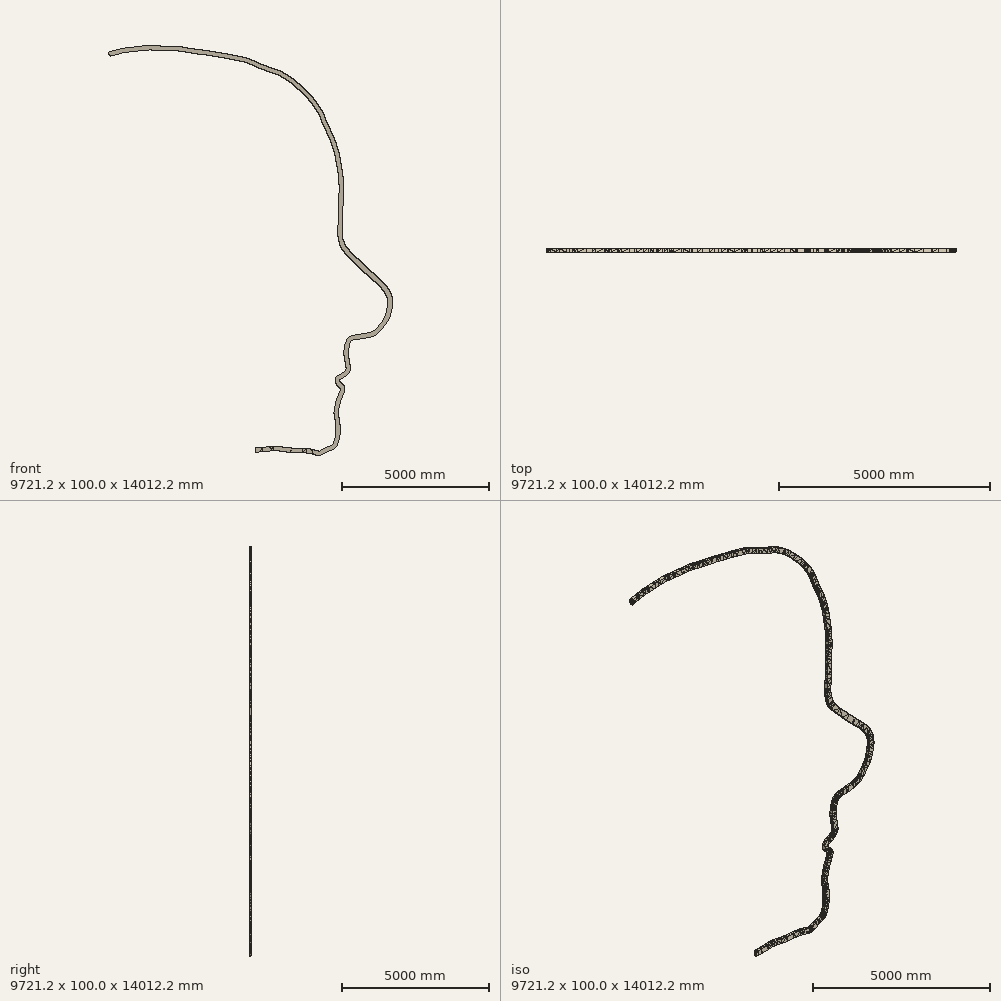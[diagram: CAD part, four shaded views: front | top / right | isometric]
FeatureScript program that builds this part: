
annotation { "Feature Type Name" : "Feature", "Feature Type Description" : "" }
export const myFeature = defineFeature(function(context is Context, id is Id, definition is map)
    precondition{}
    {
        {
            var Q0;
            Q0=qCreatedBy(makeId("Front.planeOp"),FACE);
            var sketch = newSketch(context, id + "F0", { "sketchPlane" : qUnion([Q0])});
            skLineSegment(sketch, "E0", {"start": v(3972.26, -824.32) * mm, "end": v(3779.27, -646.34) * mm});
            skLineSegment(sketch, "E1", {"start": v(3779.27, -646.34) * mm, "end": v(3769.31, -637.3) * mm});
            skLineSegment(sketch, "E2", {"start": v(3769.31, -637.3) * mm, "end": v(3603.88, -468.85) * mm});
            skLineSegment(sketch, "E3", {"start": v(3603.88, -468.85) * mm, "end": v(3566.98, -433.1) * mm});
            skLineSegment(sketch, "E4", {"start": v(3566.98, -433.1) * mm, "end": v(3382.58, -255.69) * mm});
            skLineSegment(sketch, "E5", {"start": v(3382.58, -255.69) * mm, "end": v(3380.14, -253.36) * mm});
            skLineSegment(sketch, "E6", {"start": v(3380.14, -253.36) * mm, "end": v(3227.02, -83.9) * mm});
            skLineSegment(sketch, "E7", {"start": v(3227.02, -83.9) * mm, "end": v(3181.68, -33.34) * mm});
            skLineSegment(sketch, "E8", {"start": v(3181.68, -33.34) * mm, "end": v(3138.16, 26.47) * mm});
            skLineSegment(sketch, "E9", {"start": v(3138.16, 26.47) * mm, "end": v(3127.38, 40.8) * mm});
            skLineSegment(sketch, "E10", {"start": v(3127.38, 40.8) * mm, "end": v(3121.17, 50.43) * mm});
            skLineSegment(sketch, "E11", {"start": v(3121.17, 50.43) * mm, "end": v(3079.1, 130.98) * mm});
            skLineSegment(sketch, "E12", {"start": v(3079.1, 130.98) * mm, "end": v(3056.52, 190.72) * mm});
            skLineSegment(sketch, "E13", {"start": v(3056.52, 190.72) * mm, "end": v(3014.85, 323.98) * mm});
            skLineSegment(sketch, "E14", {"start": v(3014.85, 323.98) * mm, "end": v(3003.42, 385.66) * mm});
            skLineSegment(sketch, "E15", {"start": v(3003.42, 385.66) * mm, "end": v(2997.38, 407.38) * mm});
            skLineSegment(sketch, "E16", {"start": v(2997.38, 407.38) * mm, "end": v(2980.84, 556.84) * mm});
            skLineSegment(sketch, "E17", {"start": v(2980.84, 556.84) * mm, "end": v(2980.65, 557.88) * mm});
            skLineSegment(sketch, "E18", {"start": v(2980.65, 557.88) * mm, "end": v(2980.53, 569.75) * mm});
            skLineSegment(sketch, "E19", {"start": v(2980.53, 569.75) * mm, "end": v(2979.3, 660.54) * mm});
            skLineSegment(sketch, "E20", {"start": v(2979.3, 660.54) * mm, "end": v(2980.22, 675.28) * mm});
            skLineSegment(sketch, "E21", {"start": v(2980.22, 675.28) * mm, "end": v(2979, 704.08) * mm});
            skLineSegment(sketch, "E22", {"start": v(2979, 704.08) * mm, "end": v(2991.56, 866.17) * mm});
            skLineSegment(sketch, "E23", {"start": v(2991.56, 866.17) * mm, "end": v(3001.68, 1021.18) * mm});
            skLineSegment(sketch, "E24", {"start": v(3001.68, 1021.18) * mm, "end": v(3005.61, 1150.84) * mm});
            skLineSegment(sketch, "E25", {"start": v(3005.61, 1150.84) * mm, "end": v(3008, 1205.13) * mm});
            skLineSegment(sketch, "E26", {"start": v(3008, 1205.13) * mm, "end": v(3007.86, 1232.13) * mm});
            skLineSegment(sketch, "E27", {"start": v(3007.86, 1232.13) * mm, "end": v(3008.6, 1500.34) * mm});
            skLineSegment(sketch, "E28", {"start": v(3008.6, 1500.34) * mm, "end": v(3010.72, 1635.8) * mm});
            skLineSegment(sketch, "E29", {"start": v(3010.72, 1635.8) * mm, "end": v(3011.72, 1678.4) * mm});
            skLineSegment(sketch, "E30", {"start": v(3011.72, 1678.4) * mm, "end": v(3016.1, 1776.05) * mm});
            skLineSegment(sketch, "E31", {"start": v(3016.1, 1776.05) * mm, "end": v(3023.13, 1920.29) * mm});
            skLineSegment(sketch, "E32", {"start": v(3023.13, 1920.29) * mm, "end": v(3028.4, 2010.83) * mm});
            skLineSegment(sketch, "E33", {"start": v(3028.4, 2010.83) * mm, "end": v(3029.3, 2054.07) * mm});
            skLineSegment(sketch, "E34", {"start": v(3029.3, 2054.07) * mm, "end": v(3028.87, 2105.86) * mm});
            skLineSegment(sketch, "E35", {"start": v(3028.87, 2105.86) * mm, "end": v(3028.95, 2113.76) * mm});
            skLineSegment(sketch, "E36", {"start": v(3028.95, 2113.76) * mm, "end": v(3028.93, 2114.83) * mm});
            skLineSegment(sketch, "E37", {"start": v(3028.93, 2114.83) * mm, "end": v(3028.85, 2117.34) * mm});
            skLineSegment(sketch, "E38", {"start": v(3028.85, 2117.34) * mm, "end": v(3028.63, 2122.4) * mm});
            skLineSegment(sketch, "E39", {"start": v(3028.63, 2122.4) * mm, "end": v(3025.85, 2236.85) * mm});
            skLineSegment(sketch, "E40", {"start": v(3025.85, 2236.85) * mm, "end": v(3019.27, 2333.14) * mm});
            skLineSegment(sketch, "E41", {"start": v(3019.27, 2333.14) * mm, "end": v(3014.35, 2454.84) * mm});
            skLineSegment(sketch, "E42", {"start": v(3014.35, 2454.84) * mm, "end": v(3009.17, 2525.23) * mm});
            skLineSegment(sketch, "E43", {"start": v(3009.17, 2525.23) * mm, "end": v(2999.77, 2601.55) * mm});
            skLineSegment(sketch, "E44", {"start": v(2999.77, 2601.55) * mm, "end": v(2999.15, 2606.38) * mm});
            skLineSegment(sketch, "E45", {"start": v(2999.15, 2606.38) * mm, "end": v(2996.37, 2623.67) * mm});
            skLineSegment(sketch, "E46", {"start": v(2996.37, 2623.67) * mm, "end": v(2939.92, 2948.67) * mm});
            skLineSegment(sketch, "E47", {"start": v(2939.92, 2948.67) * mm, "end": v(2924.68, 3037.87) * mm});
            skLineSegment(sketch, "E48", {"start": v(2924.68, 3037.87) * mm, "end": v(2915.3, 3107.38) * mm});
            skLineSegment(sketch, "E49", {"start": v(2915.3, 3107.38) * mm, "end": v(2889.1, 3252.45) * mm});
            skLineSegment(sketch, "E50", {"start": v(2889.1, 3252.45) * mm, "end": v(2884.6, 3279.42) * mm});
            skLineSegment(sketch, "E51", {"start": v(2884.6, 3279.42) * mm, "end": v(2875.96, 3316.34) * mm});
            skLineSegment(sketch, "E52", {"start": v(2875.96, 3316.34) * mm, "end": v(2876.2, 3313.02) * mm});
            skLineSegment(sketch, "E53", {"start": v(2876.2, 3313.02) * mm, "end": v(2867.58, 3345.82) * mm});
            skLineSegment(sketch, "E54", {"start": v(2867.58, 3345.82) * mm, "end": v(2844.67, 3415.38) * mm});
            skLineSegment(sketch, "E55", {"start": v(2844.67, 3415.38) * mm, "end": v(2827.61, 3467.45) * mm});
            skLineSegment(sketch, "E56", {"start": v(2827.61, 3467.45) * mm, "end": v(2812.09, 3521.46) * mm});
            skLineSegment(sketch, "E57", {"start": v(2812.09, 3521.46) * mm, "end": v(2797.48, 3569.06) * mm});
            skLineSegment(sketch, "E58", {"start": v(2797.48, 3569.06) * mm, "end": v(2765.14, 3666.56) * mm});
            skLineSegment(sketch, "E59", {"start": v(2765.14, 3666.56) * mm, "end": v(2742.38, 3726.82) * mm});
            skLineSegment(sketch, "E60", {"start": v(2742.38, 3726.82) * mm, "end": v(2725.35, 3770.91) * mm});
            skLineSegment(sketch, "E61", {"start": v(2725.35, 3770.91) * mm, "end": v(2656.42, 3924.3) * mm});
            skLineSegment(sketch, "E62", {"start": v(2656.42, 3924.3) * mm, "end": v(2639.9, 3958.92) * mm});
            skLineSegment(sketch, "E63", {"start": v(2639.9, 3958.92) * mm, "end": v(2633.1, 3973.99) * mm});
            skLineSegment(sketch, "E64", {"start": v(2633.1, 3973.99) * mm, "end": v(2613.84, 4015.32) * mm});
            skLineSegment(sketch, "E65", {"start": v(2613.84, 4015.32) * mm, "end": v(2589.35, 4066.77) * mm});
            skLineSegment(sketch, "E66", {"start": v(2589.35, 4066.77) * mm, "end": v(2556.64, 4136.94) * mm});
            skLineSegment(sketch, "E67", {"start": v(2556.64, 4136.94) * mm, "end": v(2547.28, 4156.79) * mm});
            skLineSegment(sketch, "E68", {"start": v(2547.28, 4156.79) * mm, "end": v(2545.41, 4160.18) * mm});
            skLineSegment(sketch, "E69", {"start": v(2545.41, 4160.18) * mm, "end": v(2530.68, 4192.32) * mm});
            skLineSegment(sketch, "E70", {"start": v(2530.68, 4192.32) * mm, "end": v(2526.52, 4196.93) * mm});
            skLineSegment(sketch, "E71", {"start": v(2526.52, 4196.93) * mm, "end": v(2511.45, 4227.76) * mm});
            skLineSegment(sketch, "E72", {"start": v(2511.45, 4227.76) * mm, "end": v(2492.95, 4272.02) * mm});
            skLineSegment(sketch, "E73", {"start": v(2492.95, 4272.02) * mm, "end": v(2457.92, 4357.18) * mm});
            skLineSegment(sketch, "E74", {"start": v(2457.92, 4357.18) * mm, "end": v(2429.87, 4423.94) * mm});
            skLineSegment(sketch, "E75", {"start": v(2429.87, 4423.94) * mm, "end": v(2428.51, 4428.26) * mm});
            skLineSegment(sketch, "E76", {"start": v(2428.51, 4428.26) * mm, "end": v(2407.27, 4484.6) * mm});
            skLineSegment(sketch, "E77", {"start": v(2407.27, 4484.6) * mm, "end": v(2367.75, 4583.7) * mm});
            skLineSegment(sketch, "E78", {"start": v(2367.75, 4583.7) * mm, "end": v(2350.04, 4623.65) * mm});
            skLineSegment(sketch, "E79", {"start": v(2350.04, 4623.65) * mm, "end": v(2340.66, 4642.93) * mm});
            skLineSegment(sketch, "E80", {"start": v(2340.66, 4642.93) * mm, "end": v(2310.55, 4699.05) * mm});
            skLineSegment(sketch, "E81", {"start": v(2310.55, 4699.05) * mm, "end": v(2289.12, 4737.81) * mm});
            skLineSegment(sketch, "E82", {"start": v(2289.12, 4737.81) * mm, "end": v(2281.78, 4750.14) * mm});
            skLineSegment(sketch, "E83", {"start": v(2281.78, 4750.14) * mm, "end": v(2253.96, 4793.21) * mm});
            skLineSegment(sketch, "E84", {"start": v(2253.96, 4793.21) * mm, "end": v(2166.56, 4923.2) * mm});
            skLineSegment(sketch, "E85", {"start": v(2166.56, 4923.2) * mm, "end": v(2158.06, 4935.64) * mm});
            skLineSegment(sketch, "E86", {"start": v(2158.06, 4935.64) * mm, "end": v(2083.12, 5033.59) * mm});
            skLineSegment(sketch, "E87", {"start": v(2083.12, 5033.59) * mm, "end": v(2056.5, 5068.4) * mm});
            skLineSegment(sketch, "E88", {"start": v(2056.5, 5068.4) * mm, "end": v(2022.08, 5111.38) * mm});
            skLineSegment(sketch, "E89", {"start": v(2022.08, 5111.38) * mm, "end": v(2006.56, 5130.31) * mm});
            skLineSegment(sketch, "E90", {"start": v(2006.56, 5130.31) * mm, "end": v(1938.82, 5208.36) * mm});
            skLineSegment(sketch, "E91", {"start": v(1938.82, 5208.36) * mm, "end": v(1900.64, 5249.8) * mm});
            skLineSegment(sketch, "E92", {"start": v(1900.64, 5249.8) * mm, "end": v(1723.26, 5424.37) * mm});
            skLineSegment(sketch, "E93", {"start": v(1723.26, 5424.37) * mm, "end": v(1663.3, 5482.42) * mm});
            skLineSegment(sketch, "E94", {"start": v(1663.3, 5482.42) * mm, "end": v(1639.5, 5504.81) * mm});
            skLineSegment(sketch, "E95", {"start": v(1639.5, 5504.81) * mm, "end": v(1621.41, 5520.52) * mm});
            skLineSegment(sketch, "E96", {"start": v(1621.41, 5520.52) * mm, "end": v(1477.89, 5651.1) * mm});
            skLineSegment(sketch, "E97", {"start": v(1477.89, 5651.1) * mm, "end": v(1449.95, 5675.24) * mm});
            skLineSegment(sketch, "E98", {"start": v(1449.95, 5675.24) * mm, "end": v(1383.35, 5730.76) * mm});
            skLineSegment(sketch, "E99", {"start": v(1383.35, 5730.76) * mm, "end": v(1311.46, 5784.69) * mm});
            skLineSegment(sketch, "E100", {"start": v(1311.46, 5784.69) * mm, "end": v(1296.05, 5795.72) * mm});
            skLineSegment(sketch, "E101", {"start": v(1296.05, 5795.72) * mm, "end": v(1258.83, 5818.84) * mm});
            skLineSegment(sketch, "E102", {"start": v(1258.83, 5818.84) * mm, "end": v(1223.82, 5839.55) * mm});
            skLineSegment(sketch, "E103", {"start": v(1223.82, 5839.55) * mm, "end": v(1193.56, 5858.43) * mm});
            skLineSegment(sketch, "E104", {"start": v(1193.56, 5858.43) * mm, "end": v(1062.64, 5937.28) * mm});
            skLineSegment(sketch, "E105", {"start": v(1062.64, 5937.28) * mm, "end": v(1018.58, 5963.58) * mm});
            skLineSegment(sketch, "E106", {"start": v(1018.58, 5963.58) * mm, "end": v(1007.24, 5969.89) * mm});
            skLineSegment(sketch, "E107", {"start": v(1007.24, 5969.89) * mm, "end": v(996.45, 5974.63) * mm});
            skLineSegment(sketch, "E108", {"start": v(996.45, 5974.63) * mm, "end": v(874.2, 6030.9) * mm});
            skLineSegment(sketch, "E109", {"start": v(874.2, 6030.9) * mm, "end": v(843.64, 6040.76) * mm});
            skLineSegment(sketch, "E110", {"start": v(843.64, 6040.76) * mm, "end": v(728.63, 6077.02) * mm});
            skLineSegment(sketch, "E111", {"start": v(728.63, 6077.02) * mm, "end": v(570.8, 6127.67) * mm});
            skLineSegment(sketch, "E112", {"start": v(570.8, 6127.67) * mm, "end": v(379.46, 6200) * mm});
            skLineSegment(sketch, "E113", {"start": v(379.46, 6200) * mm, "end": v(247.8, 6252.71) * mm});
            skLineSegment(sketch, "E114", {"start": v(247.8, 6252.71) * mm, "end": v(137.82, 6303.48) * mm});
            skLineSegment(sketch, "E115", {"start": v(137.82, 6303.48) * mm, "end": v(78.3, 6329.5) * mm});
            skLineSegment(sketch, "E116", {"start": v(78.3, 6329.5) * mm, "end": v(-31.33, 6375.46) * mm});
            skLineSegment(sketch, "E117", {"start": v(-31.33, 6375.46) * mm, "end": v(-46.3, 6381) * mm});
            skLineSegment(sketch, "E118", {"start": v(-46.3, 6381) * mm, "end": v(-181.75, 6432.14) * mm});
            skLineSegment(sketch, "E119", {"start": v(-181.75, 6432.14) * mm, "end": v(-182.38, 6432.34) * mm});
            skLineSegment(sketch, "E120", {"start": v(-182.38, 6432.34) * mm, "end": v(-259.74, 6454.73) * mm});
            skLineSegment(sketch, "E121", {"start": v(-259.74, 6454.73) * mm, "end": v(-363.85, 6475.57) * mm});
            skLineSegment(sketch, "E122", {"start": v(-363.85, 6475.57) * mm, "end": v(-548.48, 6513.3) * mm});
            skLineSegment(sketch, "E123", {"start": v(-548.48, 6513.3) * mm, "end": v(-606.65, 6527.06) * mm});
            skLineSegment(sketch, "E124", {"start": v(-606.65, 6527.06) * mm, "end": v(-794.8, 6560.9) * mm});
            skLineSegment(sketch, "E125", {"start": v(-794.8, 6560.9) * mm, "end": v(-826.95, 6566.3) * mm});
            skLineSegment(sketch, "E126", {"start": v(-826.95, 6566.3) * mm, "end": v(-882.75, 6576.29) * mm});
            skLineSegment(sketch, "E127", {"start": v(-882.75, 6576.29) * mm, "end": v(-1022.5, 6599.81) * mm});
            skLineSegment(sketch, "E128", {"start": v(-1022.5, 6599.81) * mm, "end": v(-1186.23, 6625.25) * mm});
            skLineSegment(sketch, "E129", {"start": v(-1186.23, 6625.25) * mm, "end": v(-1287.67, 6645.16) * mm});
            skLineSegment(sketch, "E130", {"start": v(-1287.67, 6645.16) * mm, "end": v(-1406.15, 6666.84) * mm});
            skLineSegment(sketch, "E131", {"start": v(-1406.15, 6666.84) * mm, "end": v(-1440.55, 6673.23) * mm});
            skLineSegment(sketch, "E132", {"start": v(-1440.55, 6673.23) * mm, "end": v(-1473.24, 6678.58) * mm});
            skLineSegment(sketch, "E133", {"start": v(-1473.24, 6678.58) * mm, "end": v(-1642.12, 6697.16) * mm});
            skLineSegment(sketch, "E134", {"start": v(-1642.12, 6697.16) * mm, "end": v(-1707, 6703.47) * mm});
            skLineSegment(sketch, "E135", {"start": v(-1707, 6703.47) * mm, "end": v(-1808.08, 6717.41) * mm});
            skLineSegment(sketch, "E136", {"start": v(-1808.08, 6717.41) * mm, "end": v(-1881.54, 6729.07) * mm});
            skLineSegment(sketch, "E137", {"start": v(-1881.54, 6729.07) * mm, "end": v(-1961.81, 6741.61) * mm});
            skLineSegment(sketch, "E138", {"start": v(-1961.81, 6741.61) * mm, "end": v(-2040.41, 6753.86) * mm});
            skLineSegment(sketch, "E139", {"start": v(-2040.41, 6753.86) * mm, "end": v(-2094.47, 6762.39) * mm});
            skLineSegment(sketch, "E140", {"start": v(-2094.47, 6762.39) * mm, "end": v(-2141.2, 6766.92) * mm});
            skLineSegment(sketch, "E141", {"start": v(-2141.2, 6766.92) * mm, "end": v(-2227, 6781.64) * mm});
            skLineSegment(sketch, "E142", {"start": v(-2227, 6781.64) * mm, "end": v(-2287.4, 6794.93) * mm});
            skLineSegment(sketch, "E143", {"start": v(-2287.4, 6794.93) * mm, "end": v(-2337.03, 6805.41) * mm});
            skLineSegment(sketch, "E144", {"start": v(-2337.03, 6805.41) * mm, "end": v(-2351.85, 6807.81) * mm});
            skLineSegment(sketch, "E145", {"start": v(-2351.85, 6807.81) * mm, "end": v(-2404.98, 6813.57) * mm});
            skLineSegment(sketch, "E146", {"start": v(-2404.98, 6813.57) * mm, "end": v(-2463.72, 6818.16) * mm});
            skLineSegment(sketch, "E147", {"start": v(-2463.72, 6818.16) * mm, "end": v(-2571.94, 6818.85) * mm});
            skLineSegment(sketch, "E148", {"start": v(-2571.94, 6818.85) * mm, "end": v(-2731.8, 6826.28) * mm});
            skLineSegment(sketch, "E149", {"start": v(-2731.8, 6826.28) * mm, "end": v(-2785.54, 6829.65) * mm});
            skLineSegment(sketch, "E150", {"start": v(-2785.54, 6829.65) * mm, "end": v(-2889.66, 6832.45) * mm});
            skLineSegment(sketch, "E151", {"start": v(-2889.66, 6832.45) * mm, "end": v(-2892.43, 6832.55) * mm});
            skLineSegment(sketch, "E152", {"start": v(-2892.43, 6832.55) * mm, "end": v(-2894.79, 6832.54) * mm});
            skLineSegment(sketch, "E153", {"start": v(-2894.79, 6832.54) * mm, "end": v(-2895.37, 6832.5) * mm});
            skLineSegment(sketch, "E154", {"start": v(-2895.37, 6832.5) * mm, "end": v(-2911.65, 6832.88) * mm});
            skLineSegment(sketch, "E155", {"start": v(-2911.65, 6832.88) * mm, "end": v(-3119.59, 6837.72) * mm});
            skLineSegment(sketch, "E156", {"start": v(-3119.59, 6837.72) * mm, "end": v(-3152.58, 6839.85) * mm});
            skLineSegment(sketch, "E157", {"start": v(-3152.58, 6839.85) * mm, "end": v(-3163.88, 6839.74) * mm});
            skLineSegment(sketch, "E158", {"start": v(-3163.88, 6839.74) * mm, "end": v(-3340.1, 6850.89) * mm});
            skLineSegment(sketch, "E159", {"start": v(-3340.1, 6850.89) * mm, "end": v(-3388.5, 6852.77) * mm});
            skLineSegment(sketch, "E160", {"start": v(-3388.5, 6852.77) * mm, "end": v(-3406.3, 6853.9) * mm});
            skLineSegment(sketch, "E161", {"start": v(-3406.3, 6853.9) * mm, "end": v(-3458.98, 6852.25) * mm});
            skLineSegment(sketch, "E162", {"start": v(-3458.98, 6852.25) * mm, "end": v(-3470.61, 6851.67) * mm});
            skLineSegment(sketch, "E163", {"start": v(-3470.61, 6851.67) * mm, "end": v(-3673.53, 6836.83) * mm});
            skLineSegment(sketch, "E164", {"start": v(-3673.53, 6836.83) * mm, "end": v(-3756.56, 6824.4) * mm});
            skLineSegment(sketch, "E165", {"start": v(-3756.56, 6824.4) * mm, "end": v(-3899, 6810.6) * mm});
            skLineSegment(sketch, "E166", {"start": v(-3899, 6810.6) * mm, "end": v(-4117.06, 6784.5) * mm});
            skLineSegment(sketch, "E167", {"start": v(-4117.06, 6784.5) * mm, "end": v(-4167.83, 6781.03) * mm});
            skLineSegment(sketch, "E168", {"start": v(-4167.83, 6781.03) * mm, "end": v(-4209.42, 6776.17) * mm});
            skLineSegment(sketch, "E169", {"start": v(-4209.42, 6776.17) * mm, "end": v(-4281.01, 6766.82) * mm});
            skLineSegment(sketch, "E170", {"start": v(-4281.01, 6766.82) * mm, "end": v(-4355.94, 6750.4) * mm});
            skLineSegment(sketch, "E171", {"start": v(-4355.94, 6750.4) * mm, "end": v(-4520.42, 6707.77) * mm});
            skLineSegment(sketch, "E172", {"start": v(-4520.42, 6707.77) * mm, "end": v(-4577.1, 6695.55) * mm});
            skLineSegment(sketch, "E173", {"start": v(-4577.1, 6695.55) * mm, "end": v(-4716.45, 6658.86) * mm});
            skLineSegment(sketch, "E174", {"start": v(-4716.45, 6658.86) * mm, "end": v(-4753.97, 6640.97) * mm});
            skLineSegment(sketch, "E175", {"start": v(-4753.97, 6640.97) * mm, "end": v(-4781.21, 6630.5) * mm});
            skLineSegment(sketch, "E176", {"start": v(-4781.21, 6630.5) * mm, "end": v(-4785.2, 6624.34) * mm});
            skLineSegment(sketch, "E177", {"start": v(-4785.2, 6624.34) * mm, "end": v(-4836.21, 6708.52) * mm});
            skLineSegment(sketch, "E178", {"start": v(-4836.21, 6708.52) * mm, "end": v(-4860.6, 6756.23) * mm});
            skLineSegment(sketch, "E179", {"start": v(-4860.6, 6756.23) * mm, "end": v(-4838, 6770.7) * mm});
            skLineSegment(sketch, "E180", {"start": v(-4838, 6770.7) * mm, "end": v(-4808.5, 6782.56) * mm});
            skLineSegment(sketch, "E181", {"start": v(-4808.5, 6782.56) * mm, "end": v(-4766.09, 6802.5) * mm});
            skLineSegment(sketch, "E182", {"start": v(-4766.09, 6802.5) * mm, "end": v(-4624.14, 6840.4) * mm});
            skLineSegment(sketch, "E183", {"start": v(-4624.14, 6840.4) * mm, "end": v(-4559.22, 6854.74) * mm});
            skLineSegment(sketch, "E184", {"start": v(-4559.22, 6854.74) * mm, "end": v(-4385.23, 6899.7) * mm});
            skLineSegment(sketch, "E185", {"start": v(-4385.23, 6899.7) * mm, "end": v(-4308.9, 6916.34) * mm});
            skLineSegment(sketch, "E186", {"start": v(-4308.9, 6916.34) * mm, "end": v(-4235.61, 6926.03) * mm});
            skLineSegment(sketch, "E187", {"start": v(-4235.61, 6926.03) * mm, "end": v(-4185.73, 6932.05) * mm});
            skLineSegment(sketch, "E188", {"start": v(-4185.73, 6932.05) * mm, "end": v(-4130.51, 6935.84) * mm});
            skLineSegment(sketch, "E189", {"start": v(-4130.51, 6935.84) * mm, "end": v(-3917.79, 6961.37) * mm});
            skLineSegment(sketch, "E190", {"start": v(-3917.79, 6961.37) * mm, "end": v(-3774.75, 6975.23) * mm});
            skLineSegment(sketch, "E191", {"start": v(-3774.75, 6975.23) * mm, "end": v(-3687.56, 6988.27) * mm});
            skLineSegment(sketch, "E192", {"start": v(-3687.56, 6988.27) * mm, "end": v(-3481.47, 7003.25) * mm});
            skLineSegment(sketch, "E193", {"start": v(-3481.47, 7003.25) * mm, "end": v(-3465.48, 7004.02) * mm});
            skLineSegment(sketch, "E194", {"start": v(-3465.48, 7004.02) * mm, "end": v(-3400.75, 7006.12) * mm});
            skLineSegment(sketch, "E195", {"start": v(-3400.75, 7006.12) * mm, "end": v(-3376.14, 7004.65) * mm});
            skLineSegment(sketch, "E196", {"start": v(-3376.14, 7004.65) * mm, "end": v(-3321.2, 7002.45) * mm});
            skLineSegment(sketch, "E197", {"start": v(-3321.2, 7002.45) * mm, "end": v(-3165.98, 6992.82) * mm});
            skLineSegment(sketch, "E198", {"start": v(-3165.98, 6992.82) * mm, "end": v(-3147.76, 6992.87) * mm});
            skLineSegment(sketch, "E199", {"start": v(-3147.76, 6992.87) * mm, "end": v(-3093.06, 6989.5) * mm});
            skLineSegment(sketch, "E200", {"start": v(-3093.06, 6989.5) * mm, "end": v(-2890.67, 6984.7) * mm});
            skLineSegment(sketch, "E201", {"start": v(-2890.67, 6984.7) * mm, "end": v(-2886.25, 6984.41) * mm});
            skLineSegment(sketch, "E202", {"start": v(-2886.25, 6984.41) * mm, "end": v(-2778.13, 6981.43) * mm});
            skLineSegment(sketch, "E203", {"start": v(-2778.13, 6981.43) * mm, "end": v(-2724.61, 6978.09) * mm});
            skLineSegment(sketch, "E204", {"start": v(-2724.61, 6978.09) * mm, "end": v(-2563.57, 6970.6) * mm});
            skLineSegment(sketch, "E205", {"start": v(-2563.57, 6970.6) * mm, "end": v(-2453.66, 6969.8) * mm});
            skLineSegment(sketch, "E206", {"start": v(-2453.66, 6969.8) * mm, "end": v(-2391.62, 6965.07) * mm});
            skLineSegment(sketch, "E207", {"start": v(-2391.62, 6965.07) * mm, "end": v(-2333.64, 6958.7) * mm});
            skLineSegment(sketch, "E208", {"start": v(-2333.64, 6958.7) * mm, "end": v(-2314.67, 6955.77) * mm});
            skLineSegment(sketch, "E209", {"start": v(-2314.67, 6955.77) * mm, "end": v(-2252.48, 6942.95) * mm});
            skLineSegment(sketch, "E210", {"start": v(-2252.48, 6942.95) * mm, "end": v(-2243.27, 6940.75) * mm});
            skLineSegment(sketch, "E211", {"start": v(-2243.27, 6940.75) * mm, "end": v(-2235.14, 6939.12) * mm});
            skLineSegment(sketch, "E212", {"start": v(-2235.14, 6939.12) * mm, "end": v(-2209.97, 6932.95) * mm});
            skLineSegment(sketch, "E213", {"start": v(-2209.97, 6932.95) * mm, "end": v(-2120.78, 6917.8) * mm});
            skLineSegment(sketch, "E214", {"start": v(-2120.78, 6917.8) * mm, "end": v(-2067.48, 6912.55) * mm});
            skLineSegment(sketch, "E215", {"start": v(-2067.48, 6912.55) * mm, "end": v(-1994.56, 6901.4) * mm});
            skLineSegment(sketch, "E216", {"start": v(-1994.56, 6901.4) * mm, "end": v(-1937.85, 6892.66) * mm});
            skLineSegment(sketch, "E217", {"start": v(-1937.85, 6892.66) * mm, "end": v(-1887.07, 6884.72) * mm});
            skLineSegment(sketch, "E218", {"start": v(-1887.07, 6884.72) * mm, "end": v(-1843.44, 6877.78) * mm});
            skLineSegment(sketch, "E219", {"start": v(-1843.44, 6877.78) * mm, "end": v(-1666.55, 6853.38) * mm});
            skLineSegment(sketch, "E220", {"start": v(-1666.55, 6853.38) * mm, "end": v(-1612.62, 6848.12) * mm});
            skLineSegment(sketch, "E221", {"start": v(-1612.62, 6848.12) * mm, "end": v(-1462.66, 6831.54) * mm});
            skLineSegment(sketch, "E222", {"start": v(-1462.66, 6831.54) * mm, "end": v(-1420.8, 6824.61) * mm});
            skLineSegment(sketch, "E223", {"start": v(-1420.8, 6824.61) * mm, "end": v(-1387.14, 6818.34) * mm});
            skLineSegment(sketch, "E224", {"start": v(-1387.14, 6818.34) * mm, "end": v(-1276.88, 6798.22) * mm});
            skLineSegment(sketch, "E225", {"start": v(-1276.88, 6798.22) * mm, "end": v(-1165.94, 6776.41) * mm});
            skLineSegment(sketch, "E226", {"start": v(-1165.94, 6776.41) * mm, "end": v(-994.2, 6749.77) * mm});
            skLineSegment(sketch, "E227", {"start": v(-994.2, 6749.77) * mm, "end": v(-873.37, 6729.55) * mm});
            skLineSegment(sketch, "E228", {"start": v(-873.37, 6729.55) * mm, "end": v(-779.05, 6712.59) * mm});
            skLineSegment(sketch, "E229", {"start": v(-779.05, 6712.59) * mm, "end": v(-715.43, 6701.98) * mm});
            skLineSegment(sketch, "E230", {"start": v(-715.43, 6701.98) * mm, "end": v(-578.02, 6677.21) * mm});
            skLineSegment(sketch, "E231", {"start": v(-578.02, 6677.21) * mm, "end": v(-535.65, 6667.2) * mm});
            skLineSegment(sketch, "E232", {"start": v(-535.65, 6667.2) * mm, "end": v(-414.65, 6642.48) * mm});
            skLineSegment(sketch, "E233", {"start": v(-414.65, 6642.48) * mm, "end": v(-235.25, 6606.4) * mm});
            skLineSegment(sketch, "E234", {"start": v(-235.25, 6606.4) * mm, "end": v(-163.46, 6585.66) * mm});
            skLineSegment(sketch, "E235", {"start": v(-163.46, 6585.66) * mm, "end": v(-130.47, 6574.9) * mm});
            skLineSegment(sketch, "E236", {"start": v(-130.47, 6574.9) * mm, "end": v(-85.68, 6558.84) * mm});
            skLineSegment(sketch, "E237", {"start": v(-85.68, 6558.84) * mm, "end": v(6.54, 6524.01) * mm});
            skLineSegment(sketch, "E238", {"start": v(6.54, 6524.01) * mm, "end": v(17.88, 6519.82) * mm});
            skLineSegment(sketch, "E239", {"start": v(17.88, 6519.82) * mm, "end": v(143.06, 6467.33) * mm});
            skLineSegment(sketch, "E240", {"start": v(143.06, 6467.33) * mm, "end": v(214.58, 6436.17) * mm});
            skLineSegment(sketch, "E241", {"start": v(214.58, 6436.17) * mm, "end": v(307.4, 6393.35) * mm});
            skLineSegment(sketch, "E242", {"start": v(307.4, 6393.35) * mm, "end": v(455.51, 6333.96) * mm});
            skLineSegment(sketch, "E243", {"start": v(455.51, 6333.96) * mm, "end": v(626.5, 6269.4) * mm});
            skLineSegment(sketch, "E244", {"start": v(626.5, 6269.4) * mm, "end": v(771.62, 6222.91) * mm});
            skLineSegment(sketch, "E245", {"start": v(771.62, 6222.91) * mm, "end": v(913.5, 6177.84) * mm});
            skLineSegment(sketch, "E246", {"start": v(913.5, 6177.84) * mm, "end": v(935.4, 6170.64) * mm});
            skLineSegment(sketch, "E247", {"start": v(935.4, 6170.64) * mm, "end": v(1036.9, 6123.97) * mm});
            skLineSegment(sketch, "E248", {"start": v(1036.9, 6123.97) * mm, "end": v(1077.9, 6104.5) * mm});
            skLineSegment(sketch, "E249", {"start": v(1077.9, 6104.5) * mm, "end": v(1084.59, 6101.03) * mm});
            skLineSegment(sketch, "E250", {"start": v(1084.59, 6101.03) * mm, "end": v(1268.15, 5990.84) * mm});
            skLineSegment(sketch, "E251", {"start": v(1268.15, 5990.84) * mm, "end": v(1303.74, 5968.64) * mm});
            skLineSegment(sketch, "E252", {"start": v(1303.74, 5968.64) * mm, "end": v(1343.26, 5945.28) * mm});
            skLineSegment(sketch, "E253", {"start": v(1343.26, 5945.28) * mm, "end": v(1379.97, 5922.38) * mm});
            skLineSegment(sketch, "E254", {"start": v(1379.97, 5922.38) * mm, "end": v(1398.78, 5908.94) * mm});
            skLineSegment(sketch, "E255", {"start": v(1398.78, 5908.94) * mm, "end": v(1476.7, 5850.65) * mm});
            skLineSegment(sketch, "E256", {"start": v(1476.7, 5850.65) * mm, "end": v(1546.2, 5792.8) * mm});
            skLineSegment(sketch, "E257", {"start": v(1546.2, 5792.8) * mm, "end": v(1577.24, 5766.04) * mm});
            skLineSegment(sketch, "E258", {"start": v(1577.24, 5766.04) * mm, "end": v(1726.03, 5630.73) * mm});
            skLineSegment(sketch, "E259", {"start": v(1726.03, 5630.73) * mm, "end": v(1744.2, 5614.98) * mm});
            skLineSegment(sketch, "E260", {"start": v(1744.2, 5614.98) * mm, "end": v(1768.06, 5592.53) * mm});
            skLineSegment(sketch, "E261", {"start": v(1768.06, 5592.53) * mm, "end": v(1826.25, 5536.15) * mm});
            skLineSegment(sketch, "E262", {"start": v(1826.25, 5536.15) * mm, "end": v(2010.72, 5354.47) * mm});
            skLineSegment(sketch, "E263", {"start": v(2010.72, 5354.47) * mm, "end": v(2051.65, 5310.03) * mm});
            skLineSegment(sketch, "E264", {"start": v(2051.65, 5310.03) * mm, "end": v(2123.02, 5227.87) * mm});
            skLineSegment(sketch, "E265", {"start": v(2123.02, 5227.87) * mm, "end": v(2140.47, 5206.58) * mm});
            skLineSegment(sketch, "E266", {"start": v(2140.47, 5206.58) * mm, "end": v(2180.37, 5156.73) * mm});
            skLineSegment(sketch, "E267", {"start": v(2180.37, 5156.73) * mm, "end": v(2211.35, 5116.18) * mm});
            skLineSegment(sketch, "E268", {"start": v(2211.35, 5116.18) * mm, "end": v(2283.16, 5022.36) * mm});
            skLineSegment(sketch, "E269", {"start": v(2283.16, 5022.36) * mm, "end": v(2297.27, 5001.74) * mm});
            skLineSegment(sketch, "E270", {"start": v(2297.27, 5001.74) * mm, "end": v(2381.67, 4876.15) * mm});
            skLineSegment(sketch, "E271", {"start": v(2381.67, 4876.15) * mm, "end": v(2412.92, 4827.8) * mm});
            skLineSegment(sketch, "E272", {"start": v(2412.92, 4827.8) * mm, "end": v(2419.29, 4817.07) * mm});
            skLineSegment(sketch, "E273", {"start": v(2419.29, 4817.07) * mm, "end": v(2444.6, 4771.25) * mm});
            skLineSegment(sketch, "E274", {"start": v(2444.6, 4771.25) * mm, "end": v(2473.9, 4716.62) * mm});
            skLineSegment(sketch, "E275", {"start": v(2473.9, 4716.62) * mm, "end": v(2486.81, 4690.02) * mm});
            skLineSegment(sketch, "E276", {"start": v(2486.81, 4690.02) * mm, "end": v(2505.99, 4646.98) * mm});
            skLineSegment(sketch, "E277", {"start": v(2505.99, 4646.98) * mm, "end": v(2546.64, 4545.33) * mm});
            skLineSegment(sketch, "E278", {"start": v(2546.64, 4545.33) * mm, "end": v(2568.9, 4486.45) * mm});
            skLineSegment(sketch, "E279", {"start": v(2568.9, 4486.45) * mm, "end": v(2570.77, 4480.84) * mm});
            skLineSegment(sketch, "E280", {"start": v(2570.77, 4480.84) * mm, "end": v(2598.22, 4415.59) * mm});
            skLineSegment(sketch, "E281", {"start": v(2598.22, 4415.59) * mm, "end": v(2636.96, 4319.55) * mm});
            skLineSegment(sketch, "E282", {"start": v(2636.96, 4319.55) * mm, "end": v(2646.58, 4296.3) * mm});
            skLineSegment(sketch, "E283", {"start": v(2646.58, 4296.3) * mm, "end": v(2655.98, 4277.27) * mm});
            skLineSegment(sketch, "E284", {"start": v(2655.98, 4277.27) * mm, "end": v(2668.1, 4257.22) * mm});
            skLineSegment(sketch, "E285", {"start": v(2668.1, 4257.22) * mm, "end": v(2682.16, 4226.51) * mm});
            skLineSegment(sketch, "E286", {"start": v(2682.16, 4226.51) * mm, "end": v(2684.11, 4222.93) * mm});
            skLineSegment(sketch, "E287", {"start": v(2684.11, 4222.93) * mm, "end": v(2693.83, 4202.35) * mm});
            skLineSegment(sketch, "E288", {"start": v(2693.83, 4202.35) * mm, "end": v(2727.43, 4130.28) * mm});
            skLineSegment(sketch, "E289", {"start": v(2727.43, 4130.28) * mm, "end": v(2752.37, 4077.86) * mm});
            skLineSegment(sketch, "E290", {"start": v(2752.37, 4077.86) * mm, "end": v(2771.29, 4037.28) * mm});
            skLineSegment(sketch, "E291", {"start": v(2771.29, 4037.28) * mm, "end": v(2778.06, 4022.24) * mm});
            skLineSegment(sketch, "E292", {"start": v(2778.06, 4022.24) * mm, "end": v(2794.6, 3987.5) * mm});
            skLineSegment(sketch, "E293", {"start": v(2794.6, 3987.5) * mm, "end": v(2865.8, 3828.97) * mm});
            skLineSegment(sketch, "E294", {"start": v(2865.8, 3828.97) * mm, "end": v(2884.55, 3780.4) * mm});
            skLineSegment(sketch, "E295", {"start": v(2884.55, 3780.4) * mm, "end": v(2908.67, 3716.52) * mm});
            skLineSegment(sketch, "E296", {"start": v(2908.67, 3716.52) * mm, "end": v(2942, 3616.03) * mm});
            skLineSegment(sketch, "E297", {"start": v(2942, 3616.03) * mm, "end": v(2957.05, 3567.11) * mm});
            skLineSegment(sketch, "E298", {"start": v(2957.05, 3567.11) * mm, "end": v(2972.44, 3513.62) * mm});
            skLineSegment(sketch, "E299", {"start": v(2972.44, 3513.62) * mm, "end": v(2990.34, 3458.78) * mm});
            skLineSegment(sketch, "E300", {"start": v(2990.34, 3458.78) * mm, "end": v(3010.94, 3395.47) * mm});
            skLineSegment(sketch, "E301", {"start": v(3010.94, 3395.47) * mm, "end": v(3021.35, 3356.3) * mm});
            skLineSegment(sketch, "E302", {"start": v(3021.35, 3356.3) * mm, "end": v(3023.68, 3351.77) * mm});
            skLineSegment(sketch, "E303", {"start": v(3023.68, 3351.77) * mm, "end": v(3033.15, 3311.43) * mm});
            skLineSegment(sketch, "E304", {"start": v(3033.15, 3311.43) * mm, "end": v(3038.1, 3281.95) * mm});
            skLineSegment(sketch, "E305", {"start": v(3038.1, 3281.95) * mm, "end": v(3065.23, 3132.22) * mm});
            skLineSegment(sketch, "E306", {"start": v(3065.23, 3132.22) * mm, "end": v(3074.16, 3066.12) * mm});
            skLineSegment(sketch, "E307", {"start": v(3074.16, 3066.12) * mm, "end": v(3089.7, 2975.26) * mm});
            skLineSegment(sketch, "E308", {"start": v(3089.7, 2975.26) * mm, "end": v(3144.9, 2657.36) * mm});
            skLineSegment(sketch, "E309", {"start": v(3144.9, 2657.36) * mm, "end": v(3149.57, 2628.3) * mm});
            skLineSegment(sketch, "E310", {"start": v(3149.57, 2628.3) * mm, "end": v(3150.69, 2619.46) * mm});
            skLineSegment(sketch, "E311", {"start": v(3150.69, 2619.46) * mm, "end": v(3160.52, 2539.5) * mm});
            skLineSegment(sketch, "E312", {"start": v(3160.52, 2539.5) * mm, "end": v(3165.82, 2467.58) * mm});
            skLineSegment(sketch, "E313", {"start": v(3165.82, 2467.58) * mm, "end": v(3170.96, 2342.22) * mm});
            skLineSegment(sketch, "E314", {"start": v(3170.96, 2342.22) * mm, "end": v(3177.75, 2242.37) * mm});
            skLineSegment(sketch, "E315", {"start": v(3177.75, 2242.37) * mm, "end": v(3180.5, 2130.7) * mm});
            skLineSegment(sketch, "E316", {"start": v(3180.5, 2130.7) * mm, "end": v(3180.9, 2121.35) * mm});
            skLineSegment(sketch, "E317", {"start": v(3180.9, 2121.35) * mm, "end": v(3181.04, 2116.82) * mm});
            skLineSegment(sketch, "E318", {"start": v(3181.04, 2116.82) * mm, "end": v(3181.09, 2114.85) * mm});
            skLineSegment(sketch, "E319", {"start": v(3181.09, 2114.85) * mm, "end": v(3180.93, 2099.43) * mm});
            skLineSegment(sketch, "E320", {"start": v(3180.93, 2099.43) * mm, "end": v(3181.27, 2047.07) * mm});
            skLineSegment(sketch, "E321", {"start": v(3181.27, 2047.07) * mm, "end": v(3180.47, 2007.94) * mm});
            skLineSegment(sketch, "E322", {"start": v(3180.47, 2007.94) * mm, "end": v(3175.78, 1927) * mm});
            skLineSegment(sketch, "E323", {"start": v(3175.78, 1927) * mm, "end": v(3170.05, 1809.32) * mm});
            skLineSegment(sketch, "E324", {"start": v(3170.05, 1809.32) * mm, "end": v(3164.32, 1681.54) * mm});
            skLineSegment(sketch, "E325", {"start": v(3164.32, 1681.54) * mm, "end": v(3162.98, 1624.55) * mm});
            skLineSegment(sketch, "E326", {"start": v(3162.98, 1624.55) * mm, "end": v(3161, 1496.73) * mm});
            skLineSegment(sketch, "E327", {"start": v(3161, 1496.73) * mm, "end": v(3160.29, 1238.83) * mm});
            skLineSegment(sketch, "E328", {"start": v(3160.29, 1238.83) * mm, "end": v(3160.49, 1201.04) * mm});
            skLineSegment(sketch, "E329", {"start": v(3160.49, 1201.04) * mm, "end": v(3157.13, 1125) * mm});
            skLineSegment(sketch, "E330", {"start": v(3157.13, 1125) * mm, "end": v(3153.66, 1011.3) * mm});
            skLineSegment(sketch, "E331", {"start": v(3153.66, 1011.3) * mm, "end": v(3142.8, 846.75) * mm});
            skLineSegment(sketch, "E332", {"start": v(3142.8, 846.75) * mm, "end": v(3130.83, 693.78) * mm});
            skLineSegment(sketch, "E333", {"start": v(3130.83, 693.78) * mm, "end": v(3132.47, 674.33) * mm});
            skLineSegment(sketch, "E334", {"start": v(3132.47, 674.33) * mm, "end": v(3132.06, 667.94) * mm});
            skLineSegment(sketch, "E335", {"start": v(3132.06, 667.94) * mm, "end": v(3132.56, 636.34) * mm});
            skLineSegment(sketch, "E336", {"start": v(3132.56, 636.34) * mm, "end": v(3133.12, 561.3) * mm});
            skLineSegment(sketch, "E337", {"start": v(3133.12, 561.3) * mm, "end": v(3134.44, 554.35) * mm});
            skLineSegment(sketch, "E338", {"start": v(3134.44, 554.35) * mm, "end": v(3146.22, 440.9) * mm});
            skLineSegment(sketch, "E339", {"start": v(3146.22, 440.9) * mm, "end": v(3167.3, 366.4) * mm});
            skLineSegment(sketch, "E340", {"start": v(3167.3, 366.4) * mm, "end": v(3169.02, 361.7) * mm});
            skLineSegment(sketch, "E341", {"start": v(3169.02, 361.7) * mm, "end": v(3220, 224.52) * mm});
            skLineSegment(sketch, "E342", {"start": v(3220, 224.52) * mm, "end": v(3234.98, 190.89) * mm});
            skLineSegment(sketch, "E343", {"start": v(3234.98, 190.89) * mm, "end": v(3296.43, 104.79) * mm});
            skLineSegment(sketch, "E344", {"start": v(3296.43, 104.79) * mm, "end": v(3309.3, 85.1) * mm});
            skLineSegment(sketch, "E345", {"start": v(3309.3, 85.1) * mm, "end": v(3311.9, 81.67) * mm});
            skLineSegment(sketch, "E346", {"start": v(3311.9, 81.67) * mm, "end": v(3323.17, 69.05) * mm});
            skLineSegment(sketch, "E347", {"start": v(3323.17, 69.05) * mm, "end": v(3514.53, -146.86) * mm});
            skLineSegment(sketch, "E348", {"start": v(3514.53, -146.86) * mm, "end": v(3686.62, -298.48) * mm});
            skLineSegment(sketch, "E349", {"start": v(3686.62, -298.48) * mm, "end": v(3720.82, -331.45) * mm});
            skLineSegment(sketch, "E350", {"start": v(3720.82, -331.45) * mm, "end": v(3862.91, -468.24) * mm});
            skLineSegment(sketch, "E351", {"start": v(3862.91, -468.24) * mm, "end": v(3863.64, -468.98) * mm});
            skLineSegment(sketch, "E352", {"start": v(3863.64, -468.98) * mm, "end": v(3864.95, -470.17) * mm});
            skLineSegment(sketch, "E353", {"start": v(3864.95, -470.17) * mm, "end": v(4083.56, -675.75) * mm});
            skLineSegment(sketch, "E354", {"start": v(4083.56, -675.75) * mm, "end": v(4274.28, -846.78) * mm});
            skLineSegment(sketch, "E355", {"start": v(4274.28, -846.78) * mm, "end": v(4274.88, -847.33) * mm});
            skLineSegment(sketch, "E356", {"start": v(4274.88, -847.33) * mm, "end": v(4275.2, -847.6) * mm});
            skLineSegment(sketch, "E357", {"start": v(4275.2, -847.6) * mm, "end": v(4275.41, -847.8) * mm});
            skLineSegment(sketch, "E358", {"start": v(4275.41, -847.8) * mm, "end": v(4280.47, -852.28) * mm});
            skLineSegment(sketch, "E359", {"start": v(4280.47, -852.28) * mm, "end": v(4439.84, -994.84) * mm});
            skLineSegment(sketch, "E360", {"start": v(4439.84, -994.84) * mm, "end": v(4617.47, -1183.49) * mm});
            skLineSegment(sketch, "E361", {"start": v(4617.47, -1183.49) * mm, "end": v(4627.35, -1193.8) * mm});
            skLineSegment(sketch, "E362", {"start": v(4627.35, -1193.8) * mm, "end": v(4633.53, -1200.5) * mm});
            skLineSegment(sketch, "E363", {"start": v(4633.53, -1200.5) * mm, "end": v(4696.22, -1285.61) * mm});
            skLineSegment(sketch, "E364", {"start": v(4696.22, -1285.61) * mm, "end": v(4720.3, -1320) * mm});
            skLineSegment(sketch, "E365", {"start": v(4720.3, -1320) * mm, "end": v(4733.12, -1341.1) * mm});
            skLineSegment(sketch, "E366", {"start": v(4733.12, -1341.1) * mm, "end": v(4793, -1457.4) * mm});
            skLineSegment(sketch, "E367", {"start": v(4793, -1457.4) * mm, "end": v(4797.06, -1467.24) * mm});
            skLineSegment(sketch, "E368", {"start": v(4797.06, -1467.24) * mm, "end": v(4829.48, -1560.55) * mm});
            skLineSegment(sketch, "E369", {"start": v(4829.48, -1560.55) * mm, "end": v(4841.35, -1601.8) * mm});
            skLineSegment(sketch, "E370", {"start": v(4841.35, -1601.8) * mm, "end": v(4850.91, -1650.2) * mm});
            skLineSegment(sketch, "E371", {"start": v(4850.91, -1650.2) * mm, "end": v(4859.5, -1698.95) * mm});
            skLineSegment(sketch, "E372", {"start": v(4859.5, -1698.95) * mm, "end": v(4859.2, -1708.22) * mm});
            skLineSegment(sketch, "E373", {"start": v(4859.2, -1708.22) * mm, "end": v(4860.06, -1789.7) * mm});
            skLineSegment(sketch, "E374", {"start": v(4860.06, -1789.7) * mm, "end": v(4860.6, -1853.57) * mm});
            skLineSegment(sketch, "E375", {"start": v(4860.6, -1853.57) * mm, "end": v(4859.43, -1875.64) * mm});
            skLineSegment(sketch, "E376", {"start": v(4859.43, -1875.64) * mm, "end": v(4848.68, -1942.8) * mm});
            skLineSegment(sketch, "E377", {"start": v(4848.68, -1942.8) * mm, "end": v(4841.49, -1994.02) * mm});
            skLineSegment(sketch, "E378", {"start": v(4841.49, -1994.02) * mm, "end": v(4821.86, -2089.13) * mm});
            skLineSegment(sketch, "E379", {"start": v(4821.86, -2089.13) * mm, "end": v(4806.74, -2152.38) * mm});
            skLineSegment(sketch, "E380", {"start": v(4806.74, -2152.38) * mm, "end": v(4782.45, -2234.7) * mm});
            skLineSegment(sketch, "E381", {"start": v(4782.45, -2234.7) * mm, "end": v(4756.6, -2307.86) * mm});
            skLineSegment(sketch, "E382", {"start": v(4756.6, -2307.86) * mm, "end": v(4750.6, -2322.24) * mm});
            skLineSegment(sketch, "E383", {"start": v(4750.6, -2322.24) * mm, "end": v(4734.76, -2354.98) * mm});
            skLineSegment(sketch, "E384", {"start": v(4734.76, -2354.98) * mm, "end": v(4709, -2403.37) * mm});
            skLineSegment(sketch, "E385", {"start": v(4709, -2403.37) * mm, "end": v(4693.49, -2429.15) * mm});
            skLineSegment(sketch, "E386", {"start": v(4693.49, -2429.15) * mm, "end": v(4630.82, -2524.39) * mm});
            skLineSegment(sketch, "E387", {"start": v(4630.82, -2524.39) * mm, "end": v(4447.22, -2753.1) * mm});
            skLineSegment(sketch, "E388", {"start": v(4447.22, -2753.1) * mm, "end": v(4442.68, -2758.68) * mm});
            skLineSegment(sketch, "E389", {"start": v(4442.68, -2758.68) * mm, "end": v(4360.75, -2844.8) * mm});
            skLineSegment(sketch, "E390", {"start": v(4360.75, -2844.8) * mm, "end": v(4356.79, -2848.64) * mm});
            skLineSegment(sketch, "E391", {"start": v(4356.79, -2848.64) * mm, "end": v(4351.74, -2852.94) * mm});
            skLineSegment(sketch, "E392", {"start": v(4351.74, -2852.94) * mm, "end": v(4306.33, -2883.64) * mm});
            skLineSegment(sketch, "E393", {"start": v(4306.33, -2883.64) * mm, "end": v(4264.88, -2906.36) * mm});
            skLineSegment(sketch, "E394", {"start": v(4264.88, -2906.36) * mm, "end": v(4200.41, -2940.37) * mm});
            skLineSegment(sketch, "E395", {"start": v(4200.41, -2940.37) * mm, "end": v(4198.18, -2941.23) * mm});
            skLineSegment(sketch, "E396", {"start": v(4198.18, -2941.23) * mm, "end": v(4181.63, -2945.88) * mm});
            skLineSegment(sketch, "E397", {"start": v(4181.63, -2945.88) * mm, "end": v(4107.56, -2966) * mm});
            skLineSegment(sketch, "E398", {"start": v(4107.56, -2966) * mm, "end": v(4098.93, -2968.15) * mm});
            skLineSegment(sketch, "E399", {"start": v(4098.93, -2968.15) * mm, "end": v(4051.62, -2976.48) * mm});
            skLineSegment(sketch, "E400", {"start": v(4051.62, -2976.48) * mm, "end": v(3859.44, -3005.89) * mm});
            skLineSegment(sketch, "E401", {"start": v(3859.44, -3005.89) * mm, "end": v(3835.06, -3011.57) * mm});
            skLineSegment(sketch, "E402", {"start": v(3835.06, -3011.57) * mm, "end": v(3781.52, -3022.62) * mm});
            skLineSegment(sketch, "E403", {"start": v(3781.52, -3022.62) * mm, "end": v(3626.54, -3033.86) * mm});
            skLineSegment(sketch, "E404", {"start": v(3626.54, -3033.86) * mm, "end": v(3551.1, -3048.9) * mm});
            skLineSegment(sketch, "E405", {"start": v(3551.1, -3048.9) * mm, "end": v(3530.09, -3054.9) * mm});
            skLineSegment(sketch, "E406", {"start": v(3530.09, -3054.9) * mm, "end": v(3502.82, -3065.69) * mm});
            skLineSegment(sketch, "E407", {"start": v(3502.82, -3065.69) * mm, "end": v(3490.4, -3073.44) * mm});
            skLineSegment(sketch, "E408", {"start": v(3490.4, -3073.44) * mm, "end": v(3482.85, -3081.25) * mm});
            skLineSegment(sketch, "E409", {"start": v(3482.85, -3081.25) * mm, "end": v(3452.65, -3103.85) * mm});
            skLineSegment(sketch, "E410", {"start": v(3452.65, -3103.85) * mm, "end": v(3429.01, -3130.95) * mm});
            skLineSegment(sketch, "E411", {"start": v(3429.01, -3130.95) * mm, "end": v(3413.85, -3150.45) * mm});
            skLineSegment(sketch, "E412", {"start": v(3413.85, -3150.45) * mm, "end": v(3402.83, -3185.62) * mm});
            skLineSegment(sketch, "E413", {"start": v(3402.83, -3185.62) * mm, "end": v(3387.62, -3234.95) * mm});
            skLineSegment(sketch, "E414", {"start": v(3387.62, -3234.95) * mm, "end": v(3376.5, -3263.64) * mm});
            skLineSegment(sketch, "E415", {"start": v(3376.5, -3263.64) * mm, "end": v(3370.2, -3320.48) * mm});
            skLineSegment(sketch, "E416", {"start": v(3370.2, -3320.48) * mm, "end": v(3366.42, -3334.79) * mm});
            skLineSegment(sketch, "E417", {"start": v(3366.42, -3334.79) * mm, "end": v(3354.96, -3370.07) * mm});
            skLineSegment(sketch, "E418", {"start": v(3354.96, -3370.07) * mm, "end": v(3351.29, -3399.25) * mm});
            skLineSegment(sketch, "E419", {"start": v(3351.29, -3399.25) * mm, "end": v(3344.1, -3460.86) * mm});
            skLineSegment(sketch, "E420", {"start": v(3344.1, -3460.86) * mm, "end": v(3344.47, -3521.34) * mm});
            skLineSegment(sketch, "E421", {"start": v(3344.47, -3521.34) * mm, "end": v(3344.48, -3533.01) * mm});
            skLineSegment(sketch, "E422", {"start": v(3344.48, -3533.01) * mm, "end": v(3345.3, -3542) * mm});
            skLineSegment(sketch, "E423", {"start": v(3345.3, -3542) * mm, "end": v(3351.47, -3607.35) * mm});
            skLineSegment(sketch, "E424", {"start": v(3351.47, -3607.35) * mm, "end": v(3369.5, -3721.06) * mm});
            skLineSegment(sketch, "E425", {"start": v(3369.5, -3721.06) * mm, "end": v(3392.84, -3858.34) * mm});
            skLineSegment(sketch, "E426", {"start": v(3392.84, -3858.34) * mm, "end": v(3415.6, -3993.67) * mm});
            skLineSegment(sketch, "E427", {"start": v(3415.6, -3993.67) * mm, "end": v(3419.64, -4027.64) * mm});
            skLineSegment(sketch, "E428", {"start": v(3419.64, -4027.64) * mm, "end": v(3421, -4049.3) * mm});
            skLineSegment(sketch, "E429", {"start": v(3421, -4049.3) * mm, "end": v(3419, -4071.98) * mm});
            skLineSegment(sketch, "E430", {"start": v(3419, -4071.98) * mm, "end": v(3409.24, -4116.16) * mm});
            skLineSegment(sketch, "E431", {"start": v(3409.24, -4116.16) * mm, "end": v(3404.44, -4135.72) * mm});
            skLineSegment(sketch, "E432", {"start": v(3404.44, -4135.72) * mm, "end": v(3399.26, -4145.78) * mm});
            skLineSegment(sketch, "E433", {"start": v(3399.26, -4145.78) * mm, "end": v(3385.19, -4172.48) * mm});
            skLineSegment(sketch, "E434", {"start": v(3385.19, -4172.48) * mm, "end": v(3346.06, -4219.36) * mm});
            skLineSegment(sketch, "E435", {"start": v(3346.06, -4219.36) * mm, "end": v(3316.5, -4250.65) * mm});
            skLineSegment(sketch, "E436", {"start": v(3316.5, -4250.65) * mm, "end": v(3293.75, -4269.04) * mm});
            skLineSegment(sketch, "E437", {"start": v(3293.75, -4269.04) * mm, "end": v(3287.12, -4273.53) * mm});
            skLineSegment(sketch, "E438", {"start": v(3287.12, -4273.53) * mm, "end": v(3239.81, -4310.73) * mm});
            skLineSegment(sketch, "E439", {"start": v(3239.81, -4310.73) * mm, "end": v(3168.37, -4356.37) * mm});
            skLineSegment(sketch, "E440", {"start": v(3168.37, -4356.37) * mm, "end": v(3159.32, -4361.8) * mm});
            skLineSegment(sketch, "E441", {"start": v(3159.32, -4361.8) * mm, "end": v(3128.4, -4377.5) * mm});
            skLineSegment(sketch, "E442", {"start": v(3128.4, -4377.5) * mm, "end": v(3051.98, -4411.14) * mm});
            skLineSegment(sketch, "E443", {"start": v(3051.98, -4411.14) * mm, "end": v(3042.2, -4424.12) * mm});
            skLineSegment(sketch, "E444", {"start": v(3042.2, -4424.12) * mm, "end": v(3037.37, -4430.71) * mm});
            skLineSegment(sketch, "E445", {"start": v(3037.37, -4430.71) * mm, "end": v(3037.82, -4439.26) * mm});
            skLineSegment(sketch, "E446", {"start": v(3037.82, -4439.26) * mm, "end": v(3039.1, -4468.45) * mm});
            skLineSegment(sketch, "E447", {"start": v(3039.1, -4468.45) * mm, "end": v(3061.65, -4496.98) * mm});
            skLineSegment(sketch, "E448", {"start": v(3061.65, -4496.98) * mm, "end": v(3081.02, -4513.9) * mm});
            skLineSegment(sketch, "E449", {"start": v(3081.02, -4513.9) * mm, "end": v(3100.38, -4532.5) * mm});
            skLineSegment(sketch, "E450", {"start": v(3100.38, -4532.5) * mm, "end": v(3128.79, -4560.62) * mm});
            skLineSegment(sketch, "E451", {"start": v(3128.79, -4560.62) * mm, "end": v(3161.52, -4589.54) * mm});
            skLineSegment(sketch, "E452", {"start": v(3161.52, -4589.54) * mm, "end": v(3179.57, -4611.49) * mm});
            skLineSegment(sketch, "E453", {"start": v(3179.57, -4611.49) * mm, "end": v(3191.3, -4623.13) * mm});
            skLineSegment(sketch, "E454", {"start": v(3191.3, -4623.13) * mm, "end": v(3201.5, -4641) * mm});
            skLineSegment(sketch, "E455", {"start": v(3201.5, -4641) * mm, "end": v(3213.16, -4674.86) * mm});
            skLineSegment(sketch, "E456", {"start": v(3213.16, -4674.86) * mm, "end": v(3220.07, -4697.65) * mm});
            skLineSegment(sketch, "E457", {"start": v(3220.07, -4697.65) * mm, "end": v(3220.42, -4706.76) * mm});
            skLineSegment(sketch, "E458", {"start": v(3220.42, -4706.76) * mm, "end": v(3226.51, -4745.18) * mm});
            skLineSegment(sketch, "E459", {"start": v(3226.51, -4745.18) * mm, "end": v(3219.16, -4785.44) * mm});
            skLineSegment(sketch, "E460", {"start": v(3219.16, -4785.44) * mm, "end": v(3217.87, -4802) * mm});
            skLineSegment(sketch, "E461", {"start": v(3217.87, -4802) * mm, "end": v(3194.57, -4880.96) * mm});
            skLineSegment(sketch, "E462", {"start": v(3194.57, -4880.96) * mm, "end": v(3191.53, -4891.73) * mm});
            skLineSegment(sketch, "E463", {"start": v(3191.53, -4891.73) * mm, "end": v(3143.55, -5003.31) * mm});
            skLineSegment(sketch, "E464", {"start": v(3143.55, -5003.31) * mm, "end": v(3127.58, -5041.66) * mm});
            skLineSegment(sketch, "E465", {"start": v(3127.58, -5041.66) * mm, "end": v(3124.94, -5047.9) * mm});
            skLineSegment(sketch, "E466", {"start": v(3124.94, -5047.9) * mm, "end": v(3119.5, -5062.47) * mm});
            skLineSegment(sketch, "E467", {"start": v(3119.5, -5062.47) * mm, "end": v(3085.8, -5151.38) * mm});
            skLineSegment(sketch, "E468", {"start": v(3085.8, -5151.38) * mm, "end": v(3073.93, -5192.46) * mm});
            skLineSegment(sketch, "E469", {"start": v(3073.93, -5192.46) * mm, "end": v(3057.1, -5265.99) * mm});
            skLineSegment(sketch, "E470", {"start": v(3057.1, -5265.99) * mm, "end": v(3029.8, -5385.9) * mm});
            skLineSegment(sketch, "E471", {"start": v(3029.8, -5385.9) * mm, "end": v(3028.04, -5391.5) * mm});
            skLineSegment(sketch, "E472", {"start": v(3028.04, -5391.5) * mm, "end": v(3024.18, -5407.46) * mm});
            skLineSegment(sketch, "E473", {"start": v(3024.18, -5407.46) * mm, "end": v(3023.3, -5411.78) * mm});
            skLineSegment(sketch, "E474", {"start": v(3023.3, -5411.78) * mm, "end": v(3012.31, -5465.78) * mm});
            skLineSegment(sketch, "E475", {"start": v(3012.31, -5465.78) * mm, "end": v(3010.75, -5497.3) * mm});
            skLineSegment(sketch, "E476", {"start": v(3010.75, -5497.3) * mm, "end": v(3005.35, -5551.39) * mm});
            skLineSegment(sketch, "E477", {"start": v(3005.35, -5551.39) * mm, "end": v(3010.69, -5613.03) * mm});
            skLineSegment(sketch, "E478", {"start": v(3010.69, -5613.03) * mm, "end": v(3016.58, -5659) * mm});
            skLineSegment(sketch, "E479", {"start": v(3016.58, -5659) * mm, "end": v(3020.3, -5675.06) * mm});
            skLineSegment(sketch, "E480", {"start": v(3020.3, -5675.06) * mm, "end": v(3036.32, -5746.69) * mm});
            skLineSegment(sketch, "E481", {"start": v(3036.32, -5746.69) * mm, "end": v(3047.31, -5809.41) * mm});
            skLineSegment(sketch, "E482", {"start": v(3047.31, -5809.41) * mm, "end": v(3052.2, -5839.36) * mm});
            skLineSegment(sketch, "E483", {"start": v(3052.2, -5839.36) * mm, "end": v(3054.49, -5861.28) * mm});
            skLineSegment(sketch, "E484", {"start": v(3054.49, -5861.28) * mm, "end": v(3058.27, -5929.15) * mm});
            skLineSegment(sketch, "E485", {"start": v(3058.27, -5929.15) * mm, "end": v(3060.64, -6010.65) * mm});
            skLineSegment(sketch, "E486", {"start": v(3060.64, -6010.65) * mm, "end": v(3061.52, -6023) * mm});
            skLineSegment(sketch, "E487", {"start": v(3061.52, -6023) * mm, "end": v(3065.91, -6143.05) * mm});
            skLineSegment(sketch, "E488", {"start": v(3065.91, -6143.05) * mm, "end": v(3067.98, -6197.53) * mm});
            skLineSegment(sketch, "E489", {"start": v(3067.98, -6197.53) * mm, "end": v(3067.97, -6208.08) * mm});
            skLineSegment(sketch, "E490", {"start": v(3067.97, -6208.08) * mm, "end": v(3067.92, -6222.9) * mm});
            skLineSegment(sketch, "E491", {"start": v(3067.92, -6222.9) * mm, "end": v(3064.14, -6273.28) * mm});
            skLineSegment(sketch, "E492", {"start": v(3064.14, -6273.28) * mm, "end": v(3054.37, -6368.24) * mm});
            skLineSegment(sketch, "E493", {"start": v(3054.37, -6368.24) * mm, "end": v(3052, -6383.58) * mm});
            skLineSegment(sketch, "E494", {"start": v(3052, -6383.58) * mm, "end": v(3049.74, -6394.58) * mm});
            skLineSegment(sketch, "E495", {"start": v(3049.74, -6394.58) * mm, "end": v(3044.01, -6422.83) * mm});
            skLineSegment(sketch, "E496", {"start": v(3044.01, -6422.83) * mm, "end": v(3031.37, -6476.6) * mm});
            skLineSegment(sketch, "E497", {"start": v(3031.37, -6476.6) * mm, "end": v(3007.35, -6548.14) * mm});
            skLineSegment(sketch, "E498", {"start": v(3007.35, -6548.14) * mm, "end": v(2980.85, -6634.6) * mm});
            skLineSegment(sketch, "E499", {"start": v(2980.85, -6634.6) * mm, "end": v(2968.38, -6661.68) * mm});
            skLineSegment(sketch, "E500", {"start": v(2968.38, -6661.68) * mm, "end": v(2965.15, -6672.31) * mm});
            skLineSegment(sketch, "E501", {"start": v(2965.15, -6672.31) * mm, "end": v(2951.68, -6695.99) * mm});
            skLineSegment(sketch, "E502", {"start": v(2951.68, -6695.99) * mm, "end": v(2931.45, -6728.2) * mm});
            skLineSegment(sketch, "E503", {"start": v(2931.45, -6728.2) * mm, "end": v(2919.5, -6739.63) * mm});
            skLineSegment(sketch, "E504", {"start": v(2919.5, -6739.63) * mm, "end": v(2896.01, -6761.33) * mm});
            skLineSegment(sketch, "E505", {"start": v(2896.01, -6761.33) * mm, "end": v(2879.74, -6773.04) * mm});
            skLineSegment(sketch, "E506", {"start": v(2879.74, -6773.04) * mm, "end": v(2845.05, -6796.95) * mm});
            skLineSegment(sketch, "E507", {"start": v(2845.05, -6796.95) * mm, "end": v(2844.43, -6797.22) * mm});
            skLineSegment(sketch, "E508", {"start": v(2844.43, -6797.22) * mm, "end": v(2839.46, -6799.05) * mm});
            skLineSegment(sketch, "E509", {"start": v(2839.46, -6799.05) * mm, "end": v(2715.25, -6844.35) * mm});
            skLineSegment(sketch, "E510", {"start": v(2715.25, -6844.35) * mm, "end": v(2704.85, -6849.33) * mm});
            skLineSegment(sketch, "E511", {"start": v(2704.85, -6849.33) * mm, "end": v(2612.59, -6890.14) * mm});
            skLineSegment(sketch, "E512", {"start": v(2612.59, -6890.14) * mm, "end": v(2477.43, -6972.55) * mm});
            skLineSegment(sketch, "E513", {"start": v(2477.43, -6972.55) * mm, "end": v(2456.83, -6984.24) * mm});
            skLineSegment(sketch, "E514", {"start": v(2456.83, -6984.24) * mm, "end": v(2427.47, -6994.84) * mm});
            skLineSegment(sketch, "E515", {"start": v(2427.47, -6994.84) * mm, "end": v(2393.38, -7005.6) * mm});
            skLineSegment(sketch, "E516", {"start": v(2393.38, -7005.6) * mm, "end": v(2345.21, -7006.12) * mm});
            skLineSegment(sketch, "E517", {"start": v(2345.21, -7006.12) * mm, "end": v(2316.22, -7003.76) * mm});
            skLineSegment(sketch, "E518", {"start": v(2316.22, -7003.76) * mm, "end": v(2273.32, -6996.87) * mm});
            skLineSegment(sketch, "E519", {"start": v(2273.32, -6996.87) * mm, "end": v(2217.16, -6984.46) * mm});
            skLineSegment(sketch, "E520", {"start": v(2217.16, -6984.46) * mm, "end": v(2145.42, -6966.1) * mm});
            skLineSegment(sketch, "E521", {"start": v(2145.42, -6966.1) * mm, "end": v(2048.87, -6940.28) * mm});
            skLineSegment(sketch, "E522", {"start": v(2048.87, -6940.28) * mm, "end": v(1995.74, -6931.2) * mm});
            skLineSegment(sketch, "E523", {"start": v(1995.74, -6931.2) * mm, "end": v(1926.53, -6920.7) * mm});
            skLineSegment(sketch, "E524", {"start": v(1926.53, -6920.7) * mm, "end": v(1903.26, -6920) * mm});
            skLineSegment(sketch, "E525", {"start": v(1903.26, -6920) * mm, "end": v(1779.6, -6911.62) * mm});
            skLineSegment(sketch, "E526", {"start": v(1779.6, -6911.62) * mm, "end": v(1615.87, -6907.5) * mm});
            skLineSegment(sketch, "E527", {"start": v(1615.87, -6907.5) * mm, "end": v(1380.54, -6900.84) * mm});
            skLineSegment(sketch, "E528", {"start": v(1380.54, -6900.84) * mm, "end": v(1379.3, -6900.83) * mm});
            skLineSegment(sketch, "E529", {"start": v(1379.3, -6900.83) * mm, "end": v(1378.45, -6900.76) * mm});
            skLineSegment(sketch, "E530", {"start": v(1378.45, -6900.76) * mm, "end": v(1377.54, -6900.7) * mm});
            skLineSegment(sketch, "E531", {"start": v(1377.54, -6900.7) * mm, "end": v(1375.97, -6900.48) * mm});
            skLineSegment(sketch, "E532", {"start": v(1375.97, -6900.48) * mm, "end": v(1189.82, -6882.37) * mm});
            skLineSegment(sketch, "E533", {"start": v(1189.82, -6882.37) * mm, "end": v(1129, -6872.6) * mm});
            skLineSegment(sketch, "E534", {"start": v(1129, -6872.6) * mm, "end": v(992.36, -6853.64) * mm});
            skLineSegment(sketch, "E535", {"start": v(992.36, -6853.64) * mm, "end": v(883.39, -6845.24) * mm});
            skLineSegment(sketch, "E536", {"start": v(883.39, -6845.24) * mm, "end": v(792.23, -6836.78) * mm});
            skLineSegment(sketch, "E537", {"start": v(792.23, -6836.78) * mm, "end": v(766.8, -6839.33) * mm});
            skLineSegment(sketch, "E538", {"start": v(766.8, -6839.33) * mm, "end": v(656.1, -6857.24) * mm});
            skLineSegment(sketch, "E539", {"start": v(656.1, -6857.24) * mm, "end": v(614.97, -6862.13) * mm});
            skLineSegment(sketch, "E540", {"start": v(614.97, -6862.13) * mm, "end": v(404.66, -6881.4) * mm});
            skLineSegment(sketch, "E541", {"start": v(404.66, -6881.4) * mm, "end": v(348.8, -6884.87) * mm});
            skLineSegment(sketch, "E542", {"start": v(348.8, -6884.87) * mm, "end": v(250.04, -6888.69) * mm});
            skLineSegment(sketch, "E543", {"start": v(250.04, -6888.69) * mm, "end": v(212.47, -6887.66) * mm});
            skLineSegment(sketch, "E544", {"start": v(212.47, -6887.66) * mm, "end": v(160.45, -6889.28) * mm});
            skLineSegment(sketch, "E545", {"start": v(160.45, -6889.28) * mm, "end": v(159.7, -6827) * mm});
            skLineSegment(sketch, "E546", {"start": v(159.7, -6827) * mm, "end": v(158.61, -6738.01) * mm});
            skLineSegment(sketch, "E547", {"start": v(158.61, -6738.01) * mm, "end": v(211.99, -6736.27) * mm});
            skLineSegment(sketch, "E548", {"start": v(211.99, -6736.27) * mm, "end": v(247.14, -6736.92) * mm});
            skLineSegment(sketch, "E549", {"start": v(247.14, -6736.92) * mm, "end": v(342.5, -6733.36) * mm});
            skLineSegment(sketch, "E550", {"start": v(342.5, -6733.36) * mm, "end": v(390.86, -6730.21) * mm});
            skLineSegment(sketch, "E551", {"start": v(390.86, -6730.21) * mm, "end": v(602.06, -6710.7) * mm});
            skLineSegment(sketch, "E552", {"start": v(602.06, -6710.7) * mm, "end": v(641.41, -6706.02) * mm});
            skLineSegment(sketch, "E553", {"start": v(641.41, -6706.02) * mm, "end": v(756.9, -6688.01) * mm});
            skLineSegment(sketch, "E554", {"start": v(756.9, -6688.01) * mm, "end": v(788.03, -6685.03) * mm});
            skLineSegment(sketch, "E555", {"start": v(788.03, -6685.03) * mm, "end": v(893.21, -6694.14) * mm});
            skLineSegment(sketch, "E556", {"start": v(893.21, -6694.14) * mm, "end": v(1023.13, -6704.14) * mm});
            skLineSegment(sketch, "E557", {"start": v(1023.13, -6704.14) * mm, "end": v(1149.25, -6721.84) * mm});
            skLineSegment(sketch, "E558", {"start": v(1149.25, -6721.84) * mm, "end": v(1204.05, -6730.29) * mm});
            skLineSegment(sketch, "E559", {"start": v(1204.05, -6730.29) * mm, "end": v(1368.45, -6746.47) * mm});
            skLineSegment(sketch, "E560", {"start": v(1368.45, -6746.47) * mm, "end": v(1382.2, -6748.34) * mm});
            skLineSegment(sketch, "E561", {"start": v(1382.2, -6748.34) * mm, "end": v(1395.68, -6749.33) * mm});
            skLineSegment(sketch, "E562", {"start": v(1395.68, -6749.33) * mm, "end": v(1406, -6749.47) * mm});
            skLineSegment(sketch, "E563", {"start": v(1406, -6749.47) * mm, "end": v(1628.83, -6755.89) * mm});
            skLineSegment(sketch, "E564", {"start": v(1628.83, -6755.89) * mm, "end": v(1786.64, -6759.89) * mm});
            skLineSegment(sketch, "E565", {"start": v(1786.64, -6759.89) * mm, "end": v(1915.75, -6768.36) * mm});
            skLineSegment(sketch, "E566", {"start": v(1915.75, -6768.36) * mm, "end": v(1942.97, -6769.27) * mm});
            skLineSegment(sketch, "E567", {"start": v(1942.97, -6769.27) * mm, "end": v(2014.82, -6780.05) * mm});
            skLineSegment(sketch, "E568", {"start": v(2014.82, -6780.05) * mm, "end": v(2080.77, -6791.24) * mm});
            skLineSegment(sketch, "E569", {"start": v(2080.77, -6791.24) * mm, "end": v(2202.37, -6823.36) * mm});
            skLineSegment(sketch, "E570", {"start": v(2202.37, -6823.36) * mm, "end": v(2241.2, -6834.72) * mm});
            skLineSegment(sketch, "E571", {"start": v(2241.2, -6834.72) * mm, "end": v(2289.97, -6845.5) * mm});
            skLineSegment(sketch, "E572", {"start": v(2289.97, -6845.5) * mm, "end": v(2331.8, -6852.44) * mm});
            skLineSegment(sketch, "E573", {"start": v(2331.8, -6852.44) * mm, "end": v(2349.72, -6855.47) * mm});
            skLineSegment(sketch, "E574", {"start": v(2349.72, -6855.47) * mm, "end": v(2368.25, -6855.61) * mm});
            skLineSegment(sketch, "E575", {"start": v(2368.25, -6855.61) * mm, "end": v(2374.8, -6853.13) * mm});
            skLineSegment(sketch, "E576", {"start": v(2374.8, -6853.13) * mm, "end": v(2394.37, -6844.1) * mm});
            skLineSegment(sketch, "E577", {"start": v(2394.37, -6844.1) * mm, "end": v(2423.4, -6827.34) * mm});
            skLineSegment(sketch, "E578", {"start": v(2423.4, -6827.34) * mm, "end": v(2536.42, -6757.72) * mm});
            skLineSegment(sketch, "E579", {"start": v(2536.42, -6757.72) * mm, "end": v(2633.32, -6714.4) * mm});
            skLineSegment(sketch, "E580", {"start": v(2633.32, -6714.4) * mm, "end": v(2654.16, -6704.41) * mm});
            skLineSegment(sketch, "E581", {"start": v(2654.16, -6704.41) * mm, "end": v(2760.39, -6666.62) * mm});
            skLineSegment(sketch, "E582", {"start": v(2760.39, -6666.62) * mm, "end": v(2772.28, -6661.84) * mm});
            skLineSegment(sketch, "E583", {"start": v(2772.28, -6661.84) * mm, "end": v(2779.88, -6658.06) * mm});
            skLineSegment(sketch, "E584", {"start": v(2779.88, -6658.06) * mm, "end": v(2794.63, -6647.16) * mm});
            skLineSegment(sketch, "E585", {"start": v(2794.63, -6647.16) * mm, "end": v(2798.83, -6644.5) * mm});
            skLineSegment(sketch, "E586", {"start": v(2798.83, -6644.5) * mm, "end": v(2808.1, -6636.46) * mm});
            skLineSegment(sketch, "E587", {"start": v(2808.1, -6636.46) * mm, "end": v(2811.98, -6633.31) * mm});
            skLineSegment(sketch, "E588", {"start": v(2811.98, -6633.31) * mm, "end": v(2825.64, -6611.08) * mm});
            skLineSegment(sketch, "E589", {"start": v(2825.64, -6611.08) * mm, "end": v(2829.3, -6603.9) * mm});
            skLineSegment(sketch, "E590", {"start": v(2829.3, -6603.9) * mm, "end": v(2831.21, -6597.4) * mm});
            skLineSegment(sketch, "E591", {"start": v(2831.21, -6597.4) * mm, "end": v(2838.15, -6582.48) * mm});
            skLineSegment(sketch, "E592", {"start": v(2838.15, -6582.48) * mm, "end": v(2855, -6527) * mm});
            skLineSegment(sketch, "E593", {"start": v(2855, -6527) * mm, "end": v(2883.2, -6441.32) * mm});
            skLineSegment(sketch, "E594", {"start": v(2883.2, -6441.32) * mm, "end": v(2898.81, -6375.5) * mm});
            skLineSegment(sketch, "E595", {"start": v(2898.81, -6375.5) * mm, "end": v(2900.45, -6367.5) * mm});
            skLineSegment(sketch, "E596", {"start": v(2900.45, -6367.5) * mm, "end": v(2901.1, -6364.4) * mm});
            skLineSegment(sketch, "E597", {"start": v(2901.1, -6364.4) * mm, "end": v(2901.7, -6360.5) * mm});
            skLineSegment(sketch, "E598", {"start": v(2901.7, -6360.5) * mm, "end": v(2910.46, -6274.63) * mm});
            skLineSegment(sketch, "E599", {"start": v(2910.46, -6274.63) * mm, "end": v(2912.66, -6246.17) * mm});
            skLineSegment(sketch, "E600", {"start": v(2912.66, -6246.17) * mm, "end": v(2912.6, -6223.63) * mm});
            skLineSegment(sketch, "E601", {"start": v(2912.6, -6223.63) * mm, "end": v(2912.62, -6206.29) * mm});
            skLineSegment(sketch, "E602", {"start": v(2912.62, -6206.29) * mm, "end": v(2911.1, -6166.56) * mm});
            skLineSegment(sketch, "E603", {"start": v(2911.1, -6166.56) * mm, "end": v(2906.8, -6056.76) * mm});
            skLineSegment(sketch, "E604", {"start": v(2906.8, -6056.76) * mm, "end": v(2905.26, -6032.3) * mm});
            skLineSegment(sketch, "E605", {"start": v(2905.26, -6032.3) * mm, "end": v(2905.24, -6015.5) * mm});
            skLineSegment(sketch, "E606", {"start": v(2905.24, -6015.5) * mm, "end": v(2905.4, -5983.58) * mm});
            skLineSegment(sketch, "E607", {"start": v(2905.4, -5983.58) * mm, "end": v(2903.68, -5921.08) * mm});
            skLineSegment(sketch, "E608", {"start": v(2903.68, -5921.08) * mm, "end": v(2900, -5849.76) * mm});
            skLineSegment(sketch, "E609", {"start": v(2900, -5849.76) * mm, "end": v(2899.97, -5849.36) * mm});
            skLineSegment(sketch, "E610", {"start": v(2899.97, -5849.36) * mm, "end": v(2899.87, -5848.76) * mm});
            skLineSegment(sketch, "E611", {"start": v(2899.87, -5848.76) * mm, "end": v(2886.8, -5775.49) * mm});
            skLineSegment(sketch, "E612", {"start": v(2886.8, -5775.49) * mm, "end": v(2868.22, -5692.44) * mm});
            skLineSegment(sketch, "E613", {"start": v(2868.22, -5692.44) * mm, "end": v(2866.55, -5685.53) * mm});
            skLineSegment(sketch, "E614", {"start": v(2866.55, -5685.53) * mm, "end": v(2866.2, -5680.7) * mm});
            skLineSegment(sketch, "E615", {"start": v(2866.2, -5680.7) * mm, "end": v(2858.57, -5617.33) * mm});
            skLineSegment(sketch, "E616", {"start": v(2858.57, -5617.33) * mm, "end": v(2853.13, -5554.03) * mm});
            skLineSegment(sketch, "E617", {"start": v(2853.13, -5554.03) * mm, "end": v(2860.29, -5476.91) * mm});
            skLineSegment(sketch, "E618", {"start": v(2860.29, -5476.91) * mm, "end": v(2862.08, -5443.61) * mm});
            skLineSegment(sketch, "E619", {"start": v(2862.08, -5443.61) * mm, "end": v(2874.85, -5379.4) * mm});
            skLineSegment(sketch, "E620", {"start": v(2874.85, -5379.4) * mm, "end": v(2875.72, -5374.88) * mm});
            skLineSegment(sketch, "E621", {"start": v(2875.72, -5374.88) * mm, "end": v(2879.2, -5360.5) * mm});
            skLineSegment(sketch, "E622", {"start": v(2879.2, -5360.5) * mm, "end": v(2880.42, -5356.83) * mm});
            skLineSegment(sketch, "E623", {"start": v(2880.42, -5356.83) * mm, "end": v(2910.25, -5226.34) * mm});
            skLineSegment(sketch, "E624", {"start": v(2910.25, -5226.34) * mm, "end": v(2928.7, -5146.4) * mm});
            skLineSegment(sketch, "E625", {"start": v(2928.7, -5146.4) * mm, "end": v(2940.14, -5107.16) * mm});
            skLineSegment(sketch, "E626", {"start": v(2940.14, -5107.16) * mm, "end": v(2970.32, -5027.33) * mm});
            skLineSegment(sketch, "E627", {"start": v(2970.32, -5027.33) * mm, "end": v(2983.26, -4992.56) * mm});
            skLineSegment(sketch, "E628", {"start": v(2983.26, -4992.56) * mm, "end": v(2989.4, -4978.02) * mm});
            skLineSegment(sketch, "E629", {"start": v(2989.4, -4978.02) * mm, "end": v(3022.96, -4897.72) * mm});
            skLineSegment(sketch, "E630", {"start": v(3022.96, -4897.72) * mm, "end": v(3047.67, -4840.63) * mm});
            skLineSegment(sketch, "E631", {"start": v(3047.67, -4840.63) * mm, "end": v(3048.95, -4836.27) * mm});
            skLineSegment(sketch, "E632", {"start": v(3048.95, -4836.27) * mm, "end": v(3068.8, -4770.12) * mm});
            skLineSegment(sketch, "E633", {"start": v(3068.8, -4770.12) * mm, "end": v(3069.26, -4762.6) * mm});
            skLineSegment(sketch, "E634", {"start": v(3069.26, -4762.6) * mm, "end": v(3074.52, -4744.2) * mm});
            skLineSegment(sketch, "E635", {"start": v(3074.52, -4744.2) * mm, "end": v(3071.66, -4733.7) * mm});
            skLineSegment(sketch, "E636", {"start": v(3071.66, -4733.7) * mm, "end": v(3071.64, -4729.99) * mm});
            skLineSegment(sketch, "E637", {"start": v(3071.64, -4729.99) * mm, "end": v(3069.25, -4722.02) * mm});
            skLineSegment(sketch, "E638", {"start": v(3069.25, -4722.02) * mm, "end": v(3065.96, -4709.26) * mm});
            skLineSegment(sketch, "E639", {"start": v(3065.96, -4709.26) * mm, "end": v(3062.57, -4703.33) * mm});
            skLineSegment(sketch, "E640", {"start": v(3062.57, -4703.33) * mm, "end": v(3057.48, -4700.24) * mm});
            skLineSegment(sketch, "E641", {"start": v(3057.48, -4700.24) * mm, "end": v(3053.67, -4696.76) * mm});
            skLineSegment(sketch, "E642", {"start": v(3053.67, -4696.76) * mm, "end": v(3026.48, -4673.03) * mm});
            skLineSegment(sketch, "E643", {"start": v(3026.48, -4673.03) * mm, "end": v(2998.81, -4645.47) * mm});
            skLineSegment(sketch, "E644", {"start": v(2998.81, -4645.47) * mm, "end": v(2963.08, -4606.62) * mm});
            skLineSegment(sketch, "E645", {"start": v(2963.08, -4606.62) * mm, "end": v(2939.21, -4582.9) * mm});
            skLineSegment(sketch, "E646", {"start": v(2939.21, -4582.9) * mm, "end": v(2906.88, -4541.4) * mm});
            skLineSegment(sketch, "E647", {"start": v(2906.88, -4541.4) * mm, "end": v(2892.91, -4388.62) * mm});
            skLineSegment(sketch, "E648", {"start": v(2892.91, -4388.62) * mm, "end": v(2892.36, -4382.97) * mm});
            skLineSegment(sketch, "E649", {"start": v(2892.36, -4382.97) * mm, "end": v(2899.01, -4376.09) * mm});
            skLineSegment(sketch, "E650", {"start": v(2899.01, -4376.09) * mm, "end": v(2973.28, -4282.13) * mm});
            skLineSegment(sketch, "E651", {"start": v(2973.28, -4282.13) * mm, "end": v(3053.44, -4245.95) * mm});
            skLineSegment(sketch, "E652", {"start": v(3053.44, -4245.95) * mm, "end": v(3087.41, -4227.96) * mm});
            skLineSegment(sketch, "E653", {"start": v(3087.41, -4227.96) * mm, "end": v(3094.07, -4223.97) * mm});
            skLineSegment(sketch, "E654", {"start": v(3094.07, -4223.97) * mm, "end": v(3154.89, -4185.02) * mm});
            skLineSegment(sketch, "E655", {"start": v(3154.89, -4185.02) * mm, "end": v(3190.04, -4157.08) * mm});
            skLineSegment(sketch, "E656", {"start": v(3190.04, -4157.08) * mm, "end": v(3193.57, -4154.71) * mm});
            skLineSegment(sketch, "E657", {"start": v(3193.57, -4154.71) * mm, "end": v(3209.2, -4142.43) * mm});
            skLineSegment(sketch, "E658", {"start": v(3209.2, -4142.43) * mm, "end": v(3235.13, -4115.82) * mm});
            skLineSegment(sketch, "E659", {"start": v(3235.13, -4115.82) * mm, "end": v(3258.18, -4088.58) * mm});
            skLineSegment(sketch, "E660", {"start": v(3258.18, -4088.58) * mm, "end": v(3260.05, -4085.9) * mm});
            skLineSegment(sketch, "E661", {"start": v(3260.05, -4085.9) * mm, "end": v(3262.34, -4081.6) * mm});
            skLineSegment(sketch, "E662", {"start": v(3262.34, -4081.6) * mm, "end": v(3264.75, -4073.58) * mm});
            skLineSegment(sketch, "E663", {"start": v(3264.75, -4073.58) * mm, "end": v(3268.48, -4053.8) * mm});
            skLineSegment(sketch, "E664", {"start": v(3268.48, -4053.8) * mm, "end": v(3268.92, -4044.89) * mm});
            skLineSegment(sketch, "E665", {"start": v(3268.92, -4044.89) * mm, "end": v(3268.02, -4037.07) * mm});
            skLineSegment(sketch, "E666", {"start": v(3268.02, -4037.07) * mm, "end": v(3265.1, -4016.87) * mm});
            skLineSegment(sketch, "E667", {"start": v(3265.1, -4016.87) * mm, "end": v(3237.77, -3855.2) * mm});
            skLineSegment(sketch, "E668", {"start": v(3237.77, -3855.2) * mm, "end": v(3203.54, -3653.88) * mm});
            skLineSegment(sketch, "E669", {"start": v(3203.54, -3653.88) * mm, "end": v(3199.72, -3629.8) * mm});
            skLineSegment(sketch, "E670", {"start": v(3199.72, -3629.8) * mm, "end": v(3192.13, -3549.33) * mm});
            skLineSegment(sketch, "E671", {"start": v(3192.13, -3549.33) * mm, "end": v(3191.69, -3544.26) * mm});
            skLineSegment(sketch, "E672", {"start": v(3191.69, -3544.26) * mm, "end": v(3191.66, -3537.59) * mm});
            skLineSegment(sketch, "E673", {"start": v(3191.66, -3537.59) * mm, "end": v(3191.17, -3455.58) * mm});
            skLineSegment(sketch, "E674", {"start": v(3191.17, -3455.58) * mm, "end": v(3201.17, -3368.5) * mm});
            skLineSegment(sketch, "E675", {"start": v(3201.17, -3368.5) * mm, "end": v(3204.45, -3341.23) * mm});
            skLineSegment(sketch, "E676", {"start": v(3204.45, -3341.23) * mm, "end": v(3214.32, -3308.3) * mm});
            skLineSegment(sketch, "E677", {"start": v(3214.32, -3308.3) * mm, "end": v(3222.41, -3278.08) * mm});
            skLineSegment(sketch, "E678", {"start": v(3222.41, -3278.08) * mm, "end": v(3229.25, -3225.13) * mm});
            skLineSegment(sketch, "E679", {"start": v(3229.25, -3225.13) * mm, "end": v(3242.12, -3192.22) * mm});
            skLineSegment(sketch, "E680", {"start": v(3242.12, -3192.22) * mm, "end": v(3265.96, -3121.13) * mm});
            skLineSegment(sketch, "E681", {"start": v(3265.96, -3121.13) * mm, "end": v(3280.43, -3077.45) * mm});
            skLineSegment(sketch, "E682", {"start": v(3280.43, -3077.45) * mm, "end": v(3301.43, -3049.38) * mm});
            skLineSegment(sketch, "E683", {"start": v(3301.43, -3049.38) * mm, "end": v(3342.18, -2999.76) * mm});
            skLineSegment(sketch, "E684", {"start": v(3342.18, -2999.76) * mm, "end": v(3395, -2960.6) * mm});
            skLineSegment(sketch, "E685", {"start": v(3395, -2960.6) * mm, "end": v(3408.54, -2947.64) * mm});
            skLineSegment(sketch, "E686", {"start": v(3408.54, -2947.64) * mm, "end": v(3433.36, -2931.23) * mm});
            skLineSegment(sketch, "E687", {"start": v(3433.36, -2931.23) * mm, "end": v(3484.83, -2910.9) * mm});
            skLineSegment(sketch, "E688", {"start": v(3484.83, -2910.9) * mm, "end": v(3508.81, -2903.61) * mm});
            skLineSegment(sketch, "E689", {"start": v(3508.81, -2903.61) * mm, "end": v(3590.05, -2886.04) * mm});
            skLineSegment(sketch, "E690", {"start": v(3590.05, -2886.04) * mm, "end": v(3654.29, -2885.17) * mm});
            skLineSegment(sketch, "E691", {"start": v(3654.29, -2885.17) * mm, "end": v(3754.29, -2862.09) * mm});
            skLineSegment(sketch, "E692", {"start": v(3754.29, -2862.09) * mm, "end": v(3828.48, -2845.3) * mm});
            skLineSegment(sketch, "E693", {"start": v(3828.48, -2845.3) * mm, "end": v(4005.07, -2818.11) * mm});
            skLineSegment(sketch, "E694", {"start": v(4005.07, -2818.11) * mm, "end": v(4109.33, -2800.18) * mm});
            skLineSegment(sketch, "E695", {"start": v(4109.33, -2800.18) * mm, "end": v(4115.54, -2798.48) * mm});
            skLineSegment(sketch, "E696", {"start": v(4115.54, -2798.48) * mm, "end": v(4172.8, -2776.13) * mm});
            skLineSegment(sketch, "E697", {"start": v(4172.8, -2776.13) * mm, "end": v(4185.85, -2769.3) * mm});
            skLineSegment(sketch, "E698", {"start": v(4185.85, -2769.3) * mm, "end": v(4242.66, -2737.9) * mm});
            skLineSegment(sketch, "E699", {"start": v(4242.66, -2737.9) * mm, "end": v(4243.85, -2737.12) * mm});
            skLineSegment(sketch, "E700", {"start": v(4243.85, -2737.12) * mm, "end": v(4267.98, -2715.99) * mm});
            skLineSegment(sketch, "E701", {"start": v(4267.98, -2715.99) * mm, "end": v(4285.75, -2698.56) * mm});
            skLineSegment(sketch, "E702", {"start": v(4285.75, -2698.56) * mm, "end": v(4332.16, -2649.37) * mm});
            skLineSegment(sketch, "E703", {"start": v(4332.16, -2649.37) * mm, "end": v(4474.6, -2474.9) * mm});
            skLineSegment(sketch, "E704", {"start": v(4474.6, -2474.9) * mm, "end": v(4478.33, -2470.19) * mm});
            skLineSegment(sketch, "E705", {"start": v(4478.33, -2470.19) * mm, "end": v(4536.16, -2380) * mm});
            skLineSegment(sketch, "E706", {"start": v(4536.16, -2380) * mm, "end": v(4547.8, -2363.93) * mm});
            skLineSegment(sketch, "E707", {"start": v(4547.8, -2363.93) * mm, "end": v(4568.28, -2330.03) * mm});
            skLineSegment(sketch, "E708", {"start": v(4568.28, -2330.03) * mm, "end": v(4586.3, -2295) * mm});
            skLineSegment(sketch, "E709", {"start": v(4586.3, -2295) * mm, "end": v(4593.56, -2276.96) * mm});
            skLineSegment(sketch, "E710", {"start": v(4593.56, -2276.96) * mm, "end": v(4605.52, -2242.71) * mm});
            skLineSegment(sketch, "E711", {"start": v(4605.52, -2242.71) * mm, "end": v(4621.61, -2195.92) * mm});
            skLineSegment(sketch, "E712", {"start": v(4621.61, -2195.92) * mm, "end": v(4630.29, -2166.58) * mm});
            skLineSegment(sketch, "E713", {"start": v(4630.29, -2166.58) * mm, "end": v(4640.51, -2120.17) * mm});
            skLineSegment(sketch, "E714", {"start": v(4640.51, -2120.17) * mm, "end": v(4658.67, -2031.73) * mm});
            skLineSegment(sketch, "E715", {"start": v(4658.67, -2031.73) * mm, "end": v(4683.11, -1894.44) * mm});
            skLineSegment(sketch, "E716", {"start": v(4683.11, -1894.44) * mm, "end": v(4687.66, -1862.29) * mm});
            skLineSegment(sketch, "E717", {"start": v(4687.66, -1862.29) * mm, "end": v(4692.92, -1824.99) * mm});
            skLineSegment(sketch, "E718", {"start": v(4692.92, -1824.99) * mm, "end": v(4693.9, -1815.6) * mm});
            skLineSegment(sketch, "E719", {"start": v(4693.9, -1815.6) * mm, "end": v(4692.68, -1728.18) * mm});
            skLineSegment(sketch, "E720", {"start": v(4692.68, -1728.18) * mm, "end": v(4692.5, -1720.44) * mm});
            skLineSegment(sketch, "E721", {"start": v(4692.5, -1720.44) * mm, "end": v(4691.18, -1710.62) * mm});
            skLineSegment(sketch, "E722", {"start": v(4691.18, -1710.62) * mm, "end": v(4682.84, -1665.26) * mm});
            skLineSegment(sketch, "E723", {"start": v(4682.84, -1665.26) * mm, "end": v(4680.58, -1653.68) * mm});
            skLineSegment(sketch, "E724", {"start": v(4680.58, -1653.68) * mm, "end": v(4680.14, -1651.11) * mm});
            skLineSegment(sketch, "E725", {"start": v(4680.14, -1651.11) * mm, "end": v(4677.09, -1641.5) * mm});
            skLineSegment(sketch, "E726", {"start": v(4677.09, -1641.5) * mm, "end": v(4655.9, -1579.56) * mm});
            skLineSegment(sketch, "E727", {"start": v(4655.9, -1579.56) * mm, "end": v(4629.6, -1519.52) * mm});
            skLineSegment(sketch, "E728", {"start": v(4629.6, -1519.52) * mm, "end": v(4614.64, -1487.56) * mm});
            skLineSegment(sketch, "E729", {"start": v(4614.64, -1487.56) * mm, "end": v(4608.07, -1474.6) * mm});
            skLineSegment(sketch, "E730", {"start": v(4608.07, -1474.6) * mm, "end": v(4579.93, -1427.63) * mm});
            skLineSegment(sketch, "E731", {"start": v(4579.93, -1427.63) * mm, "end": v(4454.88, -1269.08) * mm});
            skLineSegment(sketch, "E732", {"start": v(4454.88, -1269.08) * mm, "end": v(4446.59, -1258.49) * mm});
            skLineSegment(sketch, "E733", {"start": v(4446.59, -1258.49) * mm, "end": v(4438.5, -1249.01) * mm});
            skLineSegment(sketch, "E734", {"start": v(4438.5, -1249.01) * mm, "end": v(4429.4, -1238.96) * mm});
            skLineSegment(sketch, "E735", {"start": v(4429.4, -1238.96) * mm, "end": v(4351.95, -1158.01) * mm});
            skLineSegment(sketch, "E736", {"start": v(4351.95, -1158.01) * mm, "end": v(4315.38, -1125.6) * mm});
            skLineSegment(sketch, "E737", {"start": v(4315.38, -1125.6) * mm, "end": v(4249.5, -1067.83) * mm});
            skLineSegment(sketch, "E738", {"start": v(4249.5, -1067.83) * mm, "end": v(4148.27, -980.92) * mm});
            skLineSegment(sketch, "E739", {"start": v(4148.27, -980.92) * mm, "end": v(4047.52, -888.8) * mm});
            skLineSegment(sketch, "E740", {"start": v(4047.52, -888.8) * mm, "end": v(3994.45, -842.72) * mm});
            skLineSegment(sketch, "E741", {"start": v(3994.45, -842.72) * mm, "end": v(3972.26, -824.32) * mm});
            skSolve(sketch);
        }
        {
            var Q0;
            Q0=makeQuery(id+"F0.imprint","IMPRINT",FACE,{"disambiguationData":[TD([[makeQuery(id+"F0.imprint","IMPRINT",EDGE,{"derivedFrom":sQuery(id+"F0.wireOp",EDGE,"E0")}),-1.0]])]});
            extrude(context, id + "F1", {"entities" : qUnion([Q0]), "depth" : 100 * mm, "offsetDistance" : 25 * mm});
        }
    });
